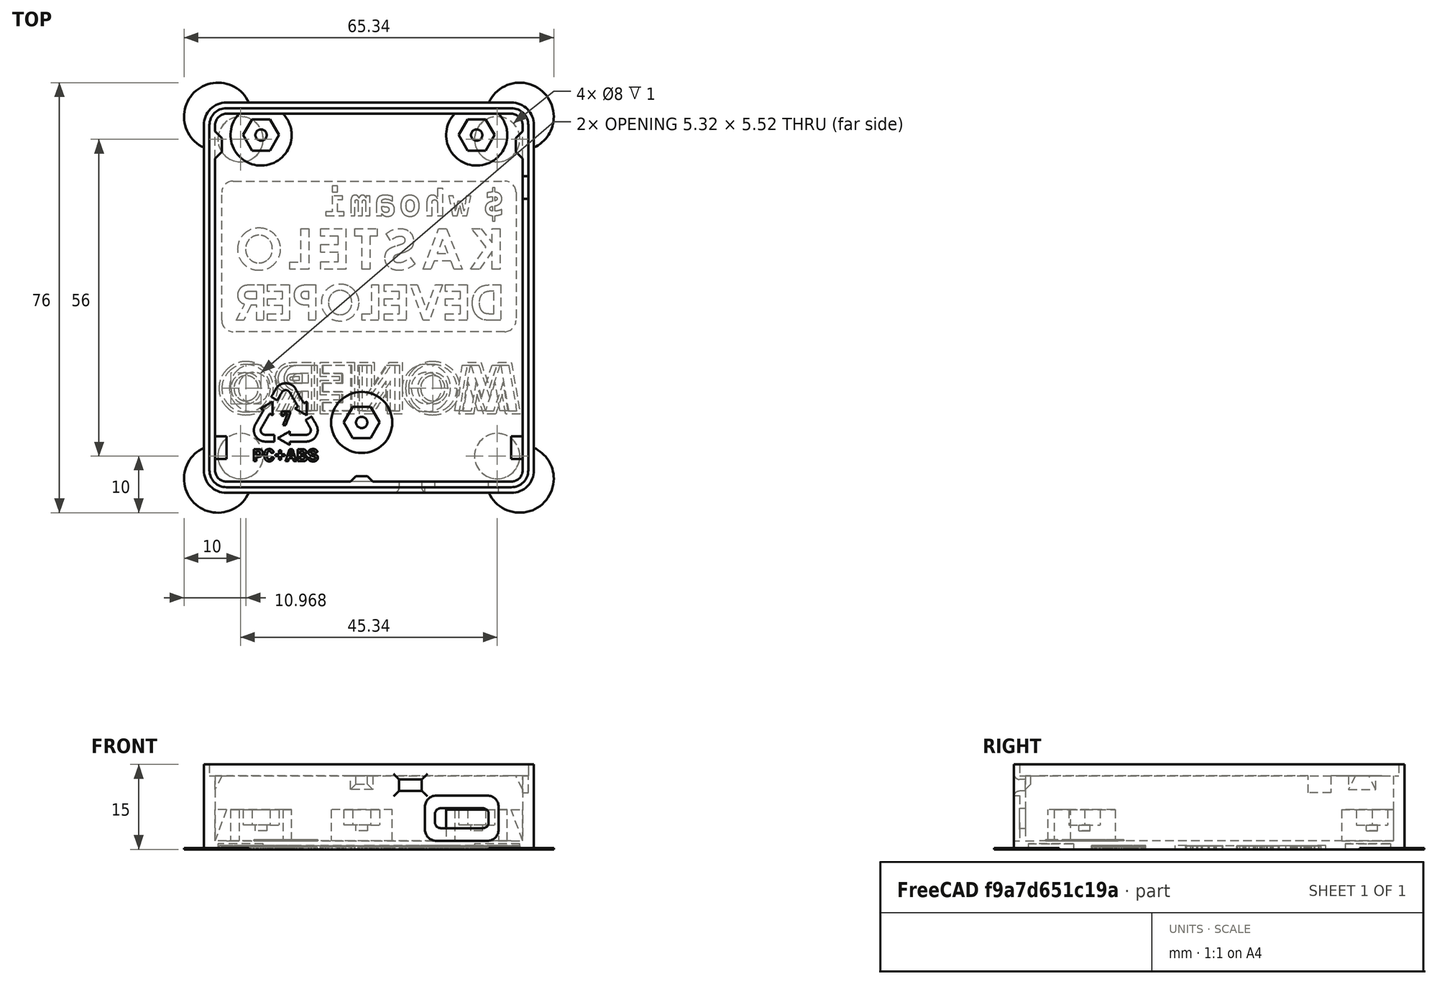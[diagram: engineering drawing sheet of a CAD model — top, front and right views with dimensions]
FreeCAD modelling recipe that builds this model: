
FCSTD DOCUMENT  (FreeCAD 0.18.3R)
Label: bneckfdmpla
License: CreativeCommons Attribution-ShareAlike
LicenseURL: http://creativecommons.org/licenses/by-sa/4.0/
objects: Sketcher::SketchObject×46, PartDesign::Pocket×29, Part::Feature×27, PartDesign::Pad×19, PartDesign::Body×14, Part::Part2DObjectPython×10, PartDesign::Fillet×6, Part::Extrusion×5, Mesh::Feature×5, App::DocumentObjectGroup×3, App::Part×3, TechDraw::DrawViewPart×3, Spreadsheet::Sheet×1, TechDraw::DrawSVGTemplate×1, TechDraw::DrawViewSymbol×1, TechDraw::DrawPage×1
note: 204 computed .brp shape members not serialized (recipe doc carries the construction recipe); baked Part::Feature solids carry a one-line shape summary decoded from their .brp

FEATURE [Sketcher::SketchObject] Sketch  label="Outline"
  MapMode = 5
  Support = -> [XY_Plane001]
  sketch-geometry (4):
    g0: LineSegment StartX=-26.67 StartY=32 StartZ=0 EndX=26.67 EndY=32 EndZ=0
    g1: LineSegment StartX=26.67 StartY=32 StartZ=0 EndX=26.67 EndY=-32 EndZ=0
    g2: LineSegment StartX=26.67 StartY=-32 StartZ=0 EndX=-26.67 EndY=-32 EndZ=0
    g3: LineSegment StartX=-26.67 StartY=-32 StartZ=0 EndX=-26.67 EndY=32 EndZ=0
  constraints (10):
    c: Coincident(g0,g1)
    c: Coincident(g1,g2)
    c: Coincident(g2,g3)
    c: Coincident(g3,g0)
    c: Horizontal(g2)
    c: Vertical(g1)
    c: DistanceY(g3,g3) = 64  'Length'
    c: DistanceX(g0,g0) = 53.34  'Width'
    c: Symmetric(g0,g0,g-2)
    c: Symmetric(g0,g2,g-1)
FEATURE [Spreadsheet::Sheet] Spreadsheet
  cells = A1=Nozzle Size; B1(nozzlesize)==0.4mm; A2=Wall Thick; B2(wallthick)==nozzlesize * 5; A3=Wall Thin; B3(wallthin)==1mm; A4=Case Length; B4(caselength)==64mm; A5=Floor Thick; B5(floorthick)==1.5mm; A6=Case Width; B6(casewidth)==53.34mm; A7=Case Height; B7(caseheight)==floorthick + batthick + pcbthick + plateclear + platethick; A8=Batt Thick; B8(batthick)==5.5mm; A9=Nut Thick; B9(nutthick)==2.7mm; A10=Nut Rad; B10(nutrad)==3.4mm; A11=Plate Clear; B11(plateclear)==4.4mm; A12=Plate Thick; B12(platethick)==2mm; A13=PCB Thick; B13(pcbthick)==1.6mm; A14=PCB Offset; B14(pcboffset)==0.5mm; A15=Skirt Height; B15(skirthick)==0.2mm
FEATURE [Sketcher::SketchObject] Sketch001  label="Outbox"
  ExternalGeometry = -> [Sketch]
  MapMode = 5
  Support = -> [XY_Plane001]
  expr: Constraints[7] = Spreadsheet.wallthick + Spreadsheet.pcboffset
  expr: Constraints[6] = Spreadsheet.wallthick + Spreadsheet.pcboffset
  sketch-geometry (4):
    g0: LineSegment StartX=-29.17 StartY=34.5 StartZ=0 EndX=29.17 EndY=34.5 EndZ=0
    g1: LineSegment StartX=29.17 StartY=34.5 StartZ=0 EndX=29.17 EndY=-34.5 EndZ=0
    g2: LineSegment StartX=29.17 StartY=-34.5 StartZ=0 EndX=-29.17 EndY=-34.5 EndZ=0
    g3: LineSegment StartX=-29.17 StartY=-34.5 StartZ=0 EndX=-29.17 EndY=34.5 EndZ=0
  constraints (10):
    c: Coincident(g0,g1)
    c: Coincident(g1,g2)
    c: Coincident(g2,g3)
    c: Coincident(g3,g0)
    c: Horizontal(g2)
    c: Vertical(g1)
    c: DistanceX(g0,g-3) = 2.5
    c: DistanceY(g-3,g0) = 2.5
    c: Symmetric(g0,g0,g-2)
    c: Symmetric(g0,g2,g-1)
FEATURE [PartDesign::Pad] Pad  label="Padmain"
  Length = 15
  Length2 = 100
  Profile = -> Sketch001
  Type = 0
  expr: Length = Spreadsheet.caseheight
FEATURE [Sketcher::SketchObject] Sketch002
  ExternalGeometry = -> [Sketch]
  MapMode = 5
  Placement = pos=(0,0,15) rot=(0,0,1;0rad)
  Support = -> [Pad]
  expr: Constraints[9] = Spreadsheet.pcboffset
  expr: Constraints[7] = Spreadsheet.pcboffset
  sketch-geometry (4):
    g0: LineSegment StartX=-27.17 StartY=32.5 StartZ=0 EndX=27.17 EndY=32.5 EndZ=0
    g1: LineSegment StartX=27.17 StartY=32.5 StartZ=0 EndX=27.17 EndY=-32.5 EndZ=0
    g2: LineSegment StartX=27.17 StartY=-32.5 StartZ=0 EndX=-27.17 EndY=-32.5 EndZ=0
    g3: LineSegment StartX=-27.17 StartY=-32.5 StartZ=0 EndX=-27.17 EndY=32.5 EndZ=0
  constraints (10):
    c: Coincident(g0,g1)
    c: Coincident(g1,g2)
    c: Coincident(g2,g3)
    c: Coincident(g3,g0)
    c: Horizontal(g2)
    c: Vertical(g1)
    c: Symmetric(g0,g0,g-2)
    c: DistanceY(g-3,g0) = 0.5
    c: Symmetric(g0,g2,g-1)
    c: DistanceX(g0,g-3) = 0.5
FEATURE [PartDesign::Pocket] Pocket  label="Pocketwallout"
  BaseFeature = -> Pad
  Length = 13.5
  Length2 = 12
  Profile = -> Sketch002
  Type = 0
  expr: Length = Padmain.Length - Spreadsheet.floorthick
FEATURE [Sketcher::SketchObject] Sketch003
  ExternalGeometry = -> [Sketch]
  MapMode = 5
  Placement = pos=(0,0,15) rot=(0,0,1;0rad)
  Support = -> [Pocket]
  expr: Constraints[9] = Spreadsheet.wallthick / 2 + Spreadsheet.pcboffset
  expr: Constraints[7] = Spreadsheet.wallthick / 2 + Spreadsheet.pcboffset
  sketch-geometry (4):
    g0: LineSegment StartX=-28.17 StartY=33.5 StartZ=0 EndX=28.17 EndY=33.5 EndZ=0
    g1: LineSegment StartX=28.17 StartY=33.5 StartZ=0 EndX=28.17 EndY=-33.5 EndZ=0
    g2: LineSegment StartX=28.17 StartY=-33.5 StartZ=0 EndX=-28.17 EndY=-33.5 EndZ=0
    g3: LineSegment StartX=-28.17 StartY=-33.5 StartZ=0 EndX=-28.17 EndY=33.5 EndZ=0
  constraints (10):
    c: Coincident(g0,g1)
    c: Coincident(g1,g2)
    c: Coincident(g2,g3)
    c: Coincident(g3,g0)
    c: Horizontal(g2)
    c: Vertical(g1)
    c: Symmetric(g0,g0,g-2)
    c: DistanceY(g-3,g0) = 1.5
    c: Symmetric(g0,g2,g-1)
    c: DistanceX(g0,g-3) = 1.5
FEATURE [PartDesign::Pocket] Pocket001  label="Pocketwallin"
  BaseFeature = -> Pocket
  Length = 2
  Length2 = 100
  Profile = -> Sketch003
  Type = 0
  expr: Length = Spreadsheet.platethick
FEATURE [TechDraw::DrawSVGTemplate] Template
  EditableTexts = Designed_by_Name=Monero Hardware; Drawing_number=1; FC-Date=December 2019; FC-SC=Scale; FC-SH=1; FC-Title=Breakneck Enclosure; Subtitle=Hardware wallet developer edition; Weight=Weight
  Height = 210
  Orientation = 1
  Width = 297
FEATURE [Sketcher::SketchObject] Sketch005
  ExternalGeometry = -> [Sketch]
  MapMode = 5
  Placement = pos=(0,-35,0) rot=(1,0,0;1.5708rad)
  expr: Constraints[18] = Spreadsheet.floorthick + Spreadsheet.batthick - 3.25mm
  sketch-geometry (8):
    g0: LineSegment StartX=12.67 StartY=7.25 StartZ=0 EndX=20.17 EndY=7.25 EndZ=0
    g1: LineSegment StartX=21.17 StartY=6.25 StartZ=0 EndX=21.17 EndY=4.75 EndZ=0
    g2: LineSegment StartX=20.17 StartY=3.75 StartZ=0 EndX=12.67 EndY=3.75 EndZ=0
    g3: LineSegment StartX=11.67 StartY=4.75 StartZ=0 EndX=11.67 EndY=6.25 EndZ=0
    g4: ArcOfCircle CenterX=12.67 CenterY=6.25 CenterZ=0 NormalX=0 NormalY=0 NormalZ=1 AngleXU=0 Radius=1 StartAngle=1.5708 EndAngle=3.14159
    g5: ArcOfCircle CenterX=12.67 CenterY=4.75 CenterZ=0 NormalX=0 NormalY=0 NormalZ=1 AngleXU=0 Radius=1 StartAngle=3.14159 EndAngle=4.71239
    g6: ArcOfCircle CenterX=20.17 CenterY=4.75 CenterZ=0 NormalX=0 NormalY=0 NormalZ=1 AngleXU=0 Radius=1 StartAngle=4.71239 EndAngle=6.28319
    g7: ArcOfCircle CenterX=20.17 CenterY=6.25 CenterZ=0 NormalX=0 NormalY=0 NormalZ=1 AngleXU=0 Radius=1 StartAngle=3e-16 EndAngle=1.5708
  constraints (20):
    c: Horizontal(g0)
    c: Horizontal(g2)
    c: Vertical(g1)
    c: Vertical(g3)
    c: Tangent(g0,g4) = 1.5708
    c: Tangent(g3,g4) = 1.5708
    c: Tangent(g3,g5) = 1.5708
    c: Tangent(g2,g5) = 1.5708
    c: Tangent(g2,g6) = 1.5708
    c: Tangent(g1,g6) = 1.5708
    c: Tangent(g1,g7) = 1.5708
    c: Tangent(g0,g7) = 1.5708
    c: Radius(g4) = 1
    c: Equal(g4,g5)
    c: Equal(g4,g6)
    c: Equal(g4,g7)
    c: DistanceY(g2,g0) = 3.5
    c: DistanceX(g3,g1) = 9.5
    c: DistanceY(g-3,g2) = 3.75
    c: DistanceX(g1,g-3) = 5.5
FEATURE [PartDesign::Pocket] Pocket002  label="Pocketusbhole"
  BaseFeature = -> Pocket001
  Length = 3
  Length2 = 100
  Profile = -> Sketch005
  Type = 0
FEATURE [Sketcher::SketchObject] Sketch007
  AttachmentOffset = pos=(0,0,10.6) rot=(0,0,1;0rad)
  ExternalGeometry = -> [Sketch]
  MapMode = 5
  Placement = pos=(0,0,10.6) rot=(0,0,1;0rad)
  Support = -> [XY_Plane001]
  expr: AttachmentOffset.Base.z = Spreadsheet.caseheight - Spreadsheet.plateclear
  sketch-geometry (12):
    g0: LineSegment StartX=-27.97 StartY=30.2 StartZ=0 EndX=-25.77 EndY=28 EndZ=0
    g1: LineSegment StartX=-25.77 StartY=28 StartZ=0 EndX=-25.77 EndY=26 EndZ=0
    g2: LineSegment StartX=-25.77 StartY=26 StartZ=0 EndX=-27.97 EndY=23.8 EndZ=0
    g3: LineSegment StartX=-27.97 StartY=23.8 StartZ=0 EndX=-27.97 EndY=30.2 EndZ=0
    g4: LineSegment StartX=25.77 StartY=28 StartZ=0 EndX=25.77 EndY=26 EndZ=0
    g5: LineSegment StartX=25.77 StartY=26 StartZ=0 EndX=27.97 EndY=23.8 EndZ=0
    g6: LineSegment StartX=27.97 StartY=23.8 StartZ=0 EndX=27.97 EndY=30.2 EndZ=0
    g7: LineSegment StartX=27.97 StartY=30.2 StartZ=0 EndX=25.77 EndY=28 EndZ=0
    g8: LineSegment StartX=-2.27 StartY=-31.55 StartZ=0 EndX=-0.27 EndY=-31.55 EndZ=0
    g9: LineSegment StartX=-0.27 StartY=-31.55 StartZ=0 EndX=1.43 EndY=-33.25 EndZ=0
    g10: LineSegment StartX=1.43 StartY=-33.25 StartZ=0 EndX=-3.97 EndY=-33.25 EndZ=0
    g11: LineSegment StartX=-3.97 StartY=-33.25 StartZ=0 EndX=-2.27 EndY=-31.55 EndZ=0
  constraints (36):
    c: Coincident(g0,g1)
    c: Vertical(g1)
    c: Coincident(g1,g2)
    c: Coincident(g2,g3)
    c: Coincident(g3,g0)
    c: DistanceY(g1,g0) = 2
    c: Angle(g0,g1) = 2.35619
    c: Angle(g1,g2) = 2.35619
    c: Vertical(g3)
    c: DistanceX(g0,g0) = 2.2
    c: Coincident(g4,g5)
    c: Coincident(g5,g6)
    c: Coincident(g6,g7)
    c: Coincident(g7,g4)
    c: DistanceY(g4,g4) = 2
    c: Vertical(g4)
    c: Angle(g4,g7) = 2.35619
    c: Angle(g5,g4) = 2.35619
    c: Vertical(g6)
    c: DistanceX(g4,g6) = 2.2
    c: Coincident(g8,g9)
    c: Coincident(g9,g10)
    c: Coincident(g10,g11)
    c: Coincident(g11,g8)
    c: Horizontal(g10)
    c: Angle(g11,g8) = 2.35619
    c: Angle(g8,g9) = 2.35619
    c: DistanceX(g8,g8) = 2
    c: DistanceY(g9,g8) = 1.7
    c: DistanceY(g0,g-3) = 4
    c: DistanceX(g-3,g0) = 0.9
    c: DistanceY(g4,g-3) = 4
    c: DistanceX(g4,g-3) = 0.9
    c: DistanceY(g-4,g8) = 0.45
    c: Horizontal(g8)
    c: DistanceX(g-4,g8) = 24.4
FEATURE [PartDesign::Pad] Pad003  label="Padshienen"
  BaseFeature = -> Pocket002
  Length = 2.4
  Length2 = 5
  Offset = 8
  Profile = -> Sketch007
  Type = 0
  expr: Length = Spreadsheet.plateclear - Spreadsheet.platethick
FEATURE [Sketcher::SketchObject] Sketch009
  ExternalGeometry = -> [Sketch003]
  MapMode = 5
  Placement = pos=(0,0,0) rot=(0.57735,0.57735,0.57735;2.0944rad)
  Support = -> [YZ_Plane001]
  expr: Constraints[9] = Spreadsheet.platethick + 2mm
  expr: Constraints[11] = Spreadsheet.platethick - 1mm
  sketch-geometry (4):
    g0: LineSegment StartX=17.5 StartY=14 StartZ=0 EndX=21.5 EndY=14 EndZ=0
    g1: LineSegment StartX=21.5 StartY=14 StartZ=0 EndX=21.5 EndY=10 EndZ=0
    g2: LineSegment StartX=21.5 StartY=10 StartZ=0 EndX=17.5 EndY=10 EndZ=0
    g3: LineSegment StartX=17.5 StartY=10 StartZ=0 EndX=17.5 EndY=14 EndZ=0
  constraints (12):
    c: Coincident(g0,g1)
    c: Coincident(g1,g2)
    c: Coincident(g2,g3)
    c: Coincident(g3,g0)
    c: Horizontal(g0)
    c: Horizontal(g2)
    c: Vertical(g1)
    c: Vertical(g3)
    c: DistanceX(g0,g0) = 4
    c: DistanceY(g2,g0) = 4
    c: DistanceX(g0,g-3) = 12
    c: DistanceY(g0,g-3) = 1
FEATURE [PartDesign::Pocket] Pocket003  label="Pocketplatrem"
  BaseFeature = -> Pad003
  Length = 28.17
  Length2 = 100
  Profile = -> Sketch009
  Reversed = true
  Type = 0
  expr: Length = Spreadsheet.casewidth / 2 + Spreadsheet.pcboffset + Spreadsheet.wallthin
FEATURE [Sketcher::SketchObject] Sketch010
  MapMode = 5
  Placement = pos=(0,0,0) rot=(1,0,0;3.14159rad)
  expr: Constraints[11] = Spreadsheet.caselength / 2
  expr: Constraints[10] = Spreadsheet.caselength / 2
  expr: Constraints[9] = Spreadsheet.caselength / 2
  expr: Constraints[8] = Spreadsheet.casewidth / 2
  expr: Constraints[7] = Spreadsheet.casewidth / 2
  expr: Constraints[6] = Spreadsheet.casewidth / 2
  expr: Constraints[1] = Spreadsheet.caselength / 2
  expr: Constraints[0] = Spreadsheet.casewidth / 2
  sketch-geometry (4):
    g0: Circle CenterX=26.67 CenterY=32 CenterZ=0 NormalX=0 NormalY=0 NormalZ=1 AngleXU=0 Radius=6
    g1: Circle CenterX=-26.67 CenterY=32 CenterZ=0 NormalX=0 NormalY=0 NormalZ=1 AngleXU=0 Radius=6
    g2: Circle CenterX=-26.67 CenterY=-32 CenterZ=0 NormalX=0 NormalY=0 NormalZ=1 AngleXU=0 Radius=6
    g3: Circle CenterX=26.67 CenterY=-32 CenterZ=0 NormalX=0 NormalY=0 NormalZ=1 AngleXU=0 Radius=6
  constraints (12):
    c: DistanceX(g-1,g0) = 26.67
    c: DistanceY(g-1,g0) = 32
    c: Radius(g0) = 6
    c: Equal(g0,g1)
    c: Equal(g1,g2)
    c: Equal(g2,g3)
    c: DistanceX(g1,g-1) = 26.67
    c: DistanceX(g2,g-1) = 26.67
    c: DistanceX(g-1,g3) = 26.67
    c: DistanceY(g2,g-1) = 32
    c: DistanceY(g3,g-1) = 32
    c: DistanceY(g-1,g1) = 32
FEATURE [PartDesign::Pad] Pad006  label="FDMBrims"
  BaseFeature = -> Pocket003
  Length = 0.2
  Length2 = 100
  Profile = -> Sketch010
  Reversed = true
  Type = 0
  expr: Length = Spreadsheet.skirthick
FEATURE [Sketcher::SketchObject] Sketch011
  ExternalGeometry = -> [Sketch]
  MapMode = 5
  Placement = pos=(0,-34.5,0) rot=(1,0,0;1.5708rad)
  expr: Constraints[18] = Spreadsheet.floorthick + Spreadsheet.batthick - 5.5mm
  sketch-geometry (8):
    g0: LineSegment StartX=11.92 StartY=9.5 StartZ=0 EndX=20.92 EndY=9.5 EndZ=0
    g1: LineSegment StartX=22.92 StartY=7.5 StartZ=0 EndX=22.92 EndY=3.5 EndZ=0
    g2: LineSegment StartX=20.92 StartY=1.5 StartZ=0 EndX=11.92 EndY=1.5 EndZ=0
    g3: LineSegment StartX=9.92 StartY=3.5 StartZ=0 EndX=9.92 EndY=7.5 EndZ=0
    g4: ArcOfCircle CenterX=11.92 CenterY=7.5 CenterZ=0 NormalX=0 NormalY=0 NormalZ=1 AngleXU=0 Radius=2 StartAngle=1.5708 EndAngle=3.14159
    g5: ArcOfCircle CenterX=20.92 CenterY=7.5 CenterZ=0 NormalX=0 NormalY=0 NormalZ=1 AngleXU=0 Radius=2 StartAngle=0 EndAngle=1.5708
    g6: ArcOfCircle CenterX=20.92 CenterY=3.5 CenterZ=0 NormalX=0 NormalY=0 NormalZ=1 AngleXU=0 Radius=2 StartAngle=4.71239 EndAngle=6.28319
    g7: ArcOfCircle CenterX=11.92 CenterY=3.5 CenterZ=0 NormalX=0 NormalY=0 NormalZ=1 AngleXU=0 Radius=2 StartAngle=3.14159 EndAngle=4.71239
  constraints (20):
    c: Horizontal(g0)
    c: Horizontal(g2)
    c: Vertical(g1)
    c: Vertical(g3)
    c: Tangent(g0,g4) = 1.5708
    c: Tangent(g3,g4) = 1.5708
    c: Tangent(g0,g5) = 1.5708
    c: Tangent(g1,g5) = 1.5708
    c: Tangent(g1,g6) = 1.5708
    c: Tangent(g2,g6) = 1.5708
    c: Tangent(g2,g7) = 1.5708
    c: Tangent(g3,g7) = 1.5708
    c: Radius(g4) = 2
    c: Equal(g4,g5)
    c: Equal(g5,g6)
    c: Equal(g6,g7)
    c: DistanceX(g0,g0) = 9
    c: DistanceY(g1,g1) = 4
    c: DistanceY(g-1,g2) = 1.5
    c: DistanceX(g1,g-3) = 3.75
FEATURE [PartDesign::Pocket] Pocket004  label="Pocketplug"
  BaseFeature = -> Pad006
  Length = 1
  Length2 = 100
  Profile = -> Sketch011
  Type = 0
FEATURE [Sketcher::SketchObject] Sketch012
  AttachmentOffset = pos=(0,0,-24) rot=(0,0,1;0rad)
  ExternalGeometry = -> [Sketch002]
  MapMode = 5
  Placement = pos=(0,24,5.3e-15) rot=(1,0,0;1.5708rad)
  Support = -> [XZ_Plane001]
  expr: Constraints[10] = Spreadsheet.caseheight - Spreadsheet.plateclear - Spreadsheet.nutthick
  expr: Constraints[9] = Spreadsheet.caseheight - Spreadsheet.plateclear
  sketch-geometry (8):
    g0: LineSegment StartX=-23.17 StartY=10.6 StartZ=0 EndX=-23.17 EndY=18.5 EndZ=0
    g1: LineSegment StartX=-23.17 StartY=18.5 StartZ=0 EndX=-27.17 EndY=10.6 EndZ=0
    g2: LineSegment StartX=-27.17 StartY=10.6 StartZ=0 EndX=-23.17 EndY=10.6 EndZ=0
    g3: Circle [constr] CenterX=-25.17 CenterY=14.55 CenterZ=0 NormalX=0 NormalY=0 NormalZ=1 AngleXU=0 Radius=4.42747
    g4: LineSegment StartX=27.17 StartY=10.6 StartZ=0 EndX=23.17 EndY=18.5 EndZ=0
    g5: LineSegment StartX=23.17 StartY=18.5 StartZ=0 EndX=23.17 EndY=10.6 EndZ=0
    g6: LineSegment StartX=23.17 StartY=10.6 StartZ=0 EndX=27.17 EndY=10.6 EndZ=0
    g7: Circle [constr] CenterX=25.17 CenterY=14.55 CenterZ=0 NormalX=0 NormalY=0 NormalZ=1 AngleXU=0 Radius=4.42747
  constraints (23):
    c: Coincident(g0,g1)
    c: Coincident(g1,g2)
    c: Coincident(g2,g0)
    c: PointOnObject(g0,g3)
    c: PointOnObject(g1,g3)
    c: PointOnObject(g2,g3)
    c: Horizontal(g2)
    c: Angle(g0,g2) = 1.5708
    c: DistanceX(g2,g2) = 4
    c: DistanceY(g-1,g0) = 10.6
    c: DistanceY(g0,g0) = 7.9
    c: Vertical(g1,g-3)
    c: Coincident(g4,g5)
    c: Coincident(g5,g6)
    c: Coincident(g6,g4)
    c: PointOnObject(g4,g7)
    c: PointOnObject(g5,g7)
    c: PointOnObject(g6,g7)
    c: Horizontal(g6)
    c: Angle(g6,g5) = 1.5708
    c: Equal(g6,g2)
    c: Equal(g5,g0)
    c: Symmetric(g5,g0,g-2)
FEATURE [PartDesign::Pocket] Pocket005  label="Pocketschienen"
  BaseFeature = -> Pocket004
  Length = 6
  Length2 = 100
  Profile = -> Sketch012
  Type = 0
FEATURE [Sketcher::SketchObject] Sketch013
  AttachmentOffset = pos=(0,0,1) rot=(0,0,1;0rad)
  ExternalGeometry = -> [Sketch007,Sketch002]
  MapMode = 5
  Placement = pos=(1,-2e-16,2e-16) rot=(0.57735,0.57735,0.57735;2.0944rad)
  Support = -> [YZ_Plane001]
  sketch-geometry (4):
    g0: LineSegment StartX=-30.5 StartY=12.6 StartZ=0 EndX=-32.5 EndY=10.6 EndZ=0
    g1: LineSegment StartX=-32.5 StartY=10.6 StartZ=0 EndX=-30.5 EndY=10.6 EndZ=0
    g2: LineSegment StartX=-30.5 StartY=10.6 StartZ=0 EndX=-30.5 EndY=12.6 EndZ=0
    g3: Circle [constr] CenterX=-31.5 CenterY=11.6 CenterZ=0 NormalX=0 NormalY=0 NormalZ=1 AngleXU=0 Radius=1.41421
  constraints (12):
    c: Coincident(g0,g1)
    c: Coincident(g1,g2)
    c: Coincident(g2,g0)
    c: PointOnObject(g0,g3)
    c: PointOnObject(g1,g3)
    c: PointOnObject(g2,g3)
    c: Horizontal(g1)
    c: Angle(g2,g1) = 1.5708
    c: DistanceX(g1,g1) = 2
    c: DistanceY(g2,g2) = 2
    c: PointOnObject(g-3,g1)
    c: Vertical(g-4,g0)
FEATURE [PartDesign::Pocket] Pocket006  label="Pocketschienund"
  BaseFeature = -> Pocket005
  Length = 4.5
  Length2 = 100
  Profile = -> Sketch013
  Type = 0
FEATURE [Sketcher::SketchObject] Sketch014
  AttachmentOffset = pos=(0,0,7) rot=(0,0,1;0rad)
  ExternalGeometry = -> [Sketch002]
  Placement = pos=(0,0,1.5) rot=(0,0,1;0rad)
  Support = -> [XY_Plane001]
  expr: Placement.Base.z = Spreadsheet.floorthick
  expr: AttachmentOffset.Base.z = Spreadsheet.floorthick + Spreadsheet.batthick
  sketch-geometry (8):
    g0: LineSegment StartX=25.17 StartY=-24.5 StartZ=0 EndX=27.17 EndY=-24.5 EndZ=0
    g1: LineSegment StartX=27.17 StartY=-24.5 StartZ=0 EndX=27.17 EndY=-28.5 EndZ=0
    g2: LineSegment StartX=27.17 StartY=-28.5 StartZ=0 EndX=25.17 EndY=-28.5 EndZ=0
    g3: LineSegment StartX=25.17 StartY=-28.5 StartZ=0 EndX=25.17 EndY=-24.5 EndZ=0
    g4: LineSegment StartX=-27.17 StartY=-24.5 StartZ=0 EndX=-25.17 EndY=-24.5 EndZ=0
    g5: LineSegment StartX=-25.17 StartY=-24.5 StartZ=0 EndX=-25.17 EndY=-28.5 EndZ=0
    g6: LineSegment StartX=-25.17 StartY=-28.5 StartZ=0 EndX=-27.17 EndY=-28.5 EndZ=0
    g7: LineSegment StartX=-27.17 StartY=-28.5 StartZ=0 EndX=-27.17 EndY=-24.5 EndZ=0
  constraints (23):
    c: Coincident(g0,g1)
    c: Coincident(g1,g2)
    c: Coincident(g2,g3)
    c: Coincident(g3,g0)
    c: Horizontal(g0)
    c: Horizontal(g2)
    c: Vertical(g1)
    c: Vertical(g3)
    c: Coincident(g4,g5)
    c: Coincident(g5,g6)
    c: Coincident(g6,g7)
    c: Coincident(g7,g4)
    c: Horizontal(g4)
    c: Horizontal(g6)
    c: Vertical(g5)
    c: Vertical(g7)
    c: DistanceY(g3,g3) = 4
    c: DistanceX(g0,g0) = 2
    c: PointOnObject(g0,g-3)
    c: DistanceY(g-3,g1) = 4
    c: Equal(g1,g5)
    c: Equal(g0,g4)
    c: Symmetric(g5,g2,g-2)
FEATURE [Sketcher::SketchObject] Sketch016
  MapMode = 5
  Support = -> [XY_Plane001]
  sketch-geometry (4):
    g0: Circle CenterX=-22.67 CenterY=28 CenterZ=0 NormalX=0 NormalY=0 NormalZ=1 AngleXU=0 Radius=4
    g1: Circle CenterX=22.67 CenterY=28 CenterZ=0 NormalX=0 NormalY=0 NormalZ=1 AngleXU=0 Radius=4
    g2: Circle CenterX=-22.67 CenterY=-28 CenterZ=0 NormalX=0 NormalY=0 NormalZ=1 AngleXU=0 Radius=4
    g3: Circle CenterX=22.67 CenterY=-28 CenterZ=0 NormalX=0 NormalY=0 NormalZ=1 AngleXU=0 Radius=4
  constraints (9):
    c: Radius(g0) = 4
    c: Radius(g1) = 4
    c: Radius(g2) = 4
    c: Radius(g3) = 4
    c: DistanceY(g3,g-1) = 28
    c: DistanceX(g-1,g3) = 22.67
    c: Symmetric(g3,g2,g-2)
    c: Symmetric(g3,g1,g-1)
    c: Symmetric(g1,g0,g-2)
FEATURE [Sketcher::SketchObject] Sketch017
  AttachmentOffset = pos=(0,0,32) rot=(0,0,1;0rad)
  MapMode = 5
  Placement = pos=(0,-32,-7.1e-15) rot=(1,0,0;1.5708rad)
  Support = -> [XZ_Plane001]
  expr: Constraints[11] = Spreadsheet.floorthick + Spreadsheet.batthick + Spreadsheet.pcbthick + 1.75mm
  sketch-geometry (4):
    g0: LineSegment StartX=5.35 StartY=12.35 StartZ=0 EndX=9.35 EndY=12.35 EndZ=0
    g1: LineSegment StartX=9.35 StartY=12.35 StartZ=0 EndX=9.35 EndY=10.35 EndZ=0
    g2: LineSegment StartX=9.35 StartY=10.35 StartZ=0 EndX=5.35 EndY=10.35 EndZ=0
    g3: LineSegment StartX=5.35 StartY=10.35 StartZ=0 EndX=5.35 EndY=12.35 EndZ=0
  constraints (12):
    c: Coincident(g0,g1)
    c: Coincident(g1,g2)
    c: Coincident(g2,g3)
    c: Coincident(g3,g0)
    c: Horizontal(g0)
    c: Horizontal(g2)
    c: Vertical(g1)
    c: Vertical(g3)
    c: DistanceX(g2,g2) = 4
    c: DistanceY(g3,g3) = 2
    c: DistanceX(g2,g-1) = -5.35
    c: DistanceY(g-1,g2) = 10.35
FEATURE [PartDesign::Pocket] Pocket009  label="Pwrswtchpockt"
  BaseFeature = -> Pocket006
  Length = 3
  Length2 = 100
  Profile = -> Sketch017
  Reversed = true
  Type = 0
FEATURE [Sketcher::SketchObject] Sketch018
  MapMode = 5
  Support = -> [XY_Plane001]
  sketch-geometry (4):
    g0: LineSegment StartX=-26 StartY=20.6 StartZ=0 EndX=26 EndY=20.6 EndZ=0
    g1: LineSegment StartX=26 StartY=20.6 StartZ=0 EndX=26 EndY=-6 EndZ=0
    g2: LineSegment StartX=26 StartY=-6 StartZ=0 EndX=-26 EndY=-6 EndZ=0
    g3: LineSegment StartX=-26 StartY=-6 StartZ=0 EndX=-26 EndY=20.6 EndZ=0
  constraints (11):
    c: Coincident(g0,g1)
    c: Coincident(g1,g2)
    c: Coincident(g2,g3)
    c: Coincident(g3,g0)
    c: DistanceY(g3,g3) = 26.6
    c: DistanceX(g2,g2) = 52
    c: Vertical(g3)
    c: Vertical(g1)
    c: Horizontal(g0)
    c: Symmetric(g2,g1,g-2)
    c: DistanceY(g2,g-1) = 6
FEATURE [PartDesign::Pocket] Pocket010  label="Etikepockt"
  BaseFeature = -> Pocket009
  Length = 0.65
  Length2 = 100
  Profile = -> Sketch018
  Reversed = true
  Type = 0
FEATURE [PartDesign::Pocket] Pocket011  label="Bumppockt"
  BaseFeature = -> Pocket010
  Length = 1
  Length2 = 100
  Profile = -> Sketch016
  Reversed = true
  Type = 0
FEATURE [TechDraw::DrawViewSymbol] Symbol  label="Monerotxt"
  LockPosition = false
  Rotation = 0
  ScaleType = 2
  Symbol = <blob: 2754 chars omitted>
  X = 210.556
  Y = 33.5011
FEATURE [Sketcher::SketchObject] Sketch019
  MapMode = 5
  Support = -> [XY_Plane003]
  sketch-geometry (4):
    g0: LineSegment StartX=-26 StartY=20.6 StartZ=0 EndX=26 EndY=20.6 EndZ=0
    g1: LineSegment StartX=26 StartY=20.6 StartZ=0 EndX=26 EndY=-6 EndZ=0
    g2: LineSegment StartX=26 StartY=-6 StartZ=0 EndX=-26 EndY=-6 EndZ=0
    g3: LineSegment StartX=-26 StartY=-6 StartZ=0 EndX=-26 EndY=20.6 EndZ=0
  constraints (11):
    c: Coincident(g0,g1)
    c: Coincident(g1,g2)
    c: Coincident(g2,g3)
    c: Coincident(g3,g0)
    c: Horizontal(g0)
    c: Vertical(g1)
    c: Vertical(g3)
    c: DistanceY(g2,g-1) = 6
    c: DistanceY(g3,g3) = 26.6
    c: DistanceX(g2,g2) = 52
    c: Symmetric(g2,g1,g-2)
FEATURE [PartDesign::Pad] Pad008  label="Etikepad"
  Length = 0.65
  Length2 = 100
  Profile = -> Sketch019
  Type = 0
FEATURE [PartDesign::Fillet] Fillet002  label="Etikepadfil"
  Base = -> Pad008 [Edge2,Edge1,Edge8,Edge5]
  BaseFeature = -> Pad008
  Radius = 2
FEATURE [Part::Part2DObjectPython] ShapeString  label="Shapestrin-0,4mm"  # Draft 2D object (typed FeaturePython)
  FontFile = <userpath>/Downloads/MoneroGothic_v3.otf
  Placement = pos=(25,-20,0) rot=(0,1,0;3.14159rad)
  Size = 4.5
  String = MONERO
  Tracking = 0
FEATURE [Part::Part2DObjectPython] ShapeString001  label="Shapestrout"  # Draft 2D object (typed FeaturePython)
  FontFile = <userpath>/Downloads/MoneroGothic_v3.otf
  Placement = pos=(25,-20,0) rot=(0,1,0;3.14159rad)
  Size = 4.5
  String = MONERO
  Tracking = 0
FEATURE [Part::Extrusion] Extrude  label="Textstringtrude"
  Base = -> ShapeString001
  Dir = (0,0,-1)
  DirMode = 2
  FaceMakerClass = Part::FaceMakerBullseye
  LengthFwd = 0
  LengthRev = 0.4
  Solid = true
  Symmetric = false
FEATURE [Part::Part2DObjectPython] ShapeString002  label="Shapewhoami"  # Draft 2D object (typed FeaturePython)
  FontFile = <userpath>/Downloads/DejaVuSansMono-Bold.ttf
  Placement = pos=(18,14.5,0) rot=(0,1,0;3.14159rad)
  Size = 5
  String = whoami
  Tracking = 0.5
FEATURE [Part::Part2DObjectPython] ShapeString003  label="Shapekastelo"  # Draft 2D object (typed FeaturePython)
  FontFile = <userpath>/Downloads/MoneroGothic_v3.otf
  Placement = pos=(24,5,0) rot=(0,1,0;3.14159rad)
  Size = 4
  String = KASTELO
  Tracking = 1
FEATURE [Part::Part2DObjectPython] ShapeString004  label="Shapedevkit"  # Draft 2D object (typed FeaturePython)
  FontFile = <userpath>/Downloads/MoneroGothic_v3.otf
  Placement = pos=(24,-4,0) rot=(0,1,0;3.14159rad)
  Size = 3.5
  String = DEVELOPER
  Tracking = 0
FEATURE [PartDesign::Pocket] Pocket013  label="Whoamipock"
  BaseFeature = -> Fillet002
  Length = 0.6
  Length2 = 100
  Profile = -> ShapeString002
  Type = 0
FEATURE [PartDesign::Pocket] Pocket014  label="Kastelopock"
  BaseFeature = -> Pocket013
  Length = 0.6
  Length2 = 100
  Profile = -> ShapeString003
  Type = 0
FEATURE [PartDesign::Pocket] Pocket015  label="Developock"
  BaseFeature = -> Pocket014
  Length = 0.6
  Length2 = 100
  Profile = -> ShapeString004
  Type = 0
FEATURE [Part::Part2DObjectPython] ShapeString005  label="Strshawhoami"  # Draft 2D object (typed FeaturePython)
  FontFile = <userpath>/Downloads/DejaVuSansMono-Bold.ttf
  Placement = pos=(18,14.5,0) rot=(0,1,0;3.14159rad)
  Size = 5
  String = whoami
  Tracking = 0.5
FEATURE [Part::Part2DObjectPython] ShapeString006  label="Strshakastelo"  # Draft 2D object (typed FeaturePython)
  FontFile = <userpath>/Downloads/MoneroGothic_v3.otf
  Placement = pos=(24,5,0) rot=(0,1,0;3.14159rad)
  Size = 4
  String = KASTELO
  Tracking = 1
FEATURE [Part::Part2DObjectPython] ShapeString007  label="Strshadevelop"  # Draft 2D object (typed FeaturePython)
  FontFile = <userpath>/Downloads/MoneroGothic_v3.otf
  Placement = pos=(24,-4,0) rot=(0,1,0;3.14159rad)
  Size = 3.5
  String = DEVELOPER
  Tracking = 0
FEATURE [Part::Part2DObjectPython] ShapeString008  label="Shapedollar"  # Draft 2D object (typed FeaturePython)
  FontFile = <userpath>/Downloads/DejaVuSansMono-Bold.ttf
  Placement = pos=(24,14.5,0) rot=(0,1,0;3.14159rad)
  Size = 5
  String = $
  Tracking = 0
FEATURE [Part::Part2DObjectPython] ShapeString009  label="Strshadollar"  # Draft 2D object (typed FeaturePython)
  FontFile = <userpath>/Downloads/DejaVuSansMono-Bold.ttf
  Placement = pos=(24,14.5,0) rot=(0,1,0;3.14159rad)
  Size = 5
  String = $
  Tracking = 0
FEATURE [PartDesign::Pocket] Pocket016  label="Dollarpock"
  BaseFeature = -> Pocket015
  Length = 0.6
  Length2 = 100
  Profile = -> ShapeString008
  Type = 0
FEATURE [PartDesign::Body] Body001  label="Bodyetik"
  Group = -> [Sketch019,Pad008,Fillet002,ShapeString002,ShapeString003,ShapeString004,Pocket013,Pocket014,Pocket015,ShapeString008,Pocket016]
  Origin = -> Origin003
  Tip = -> Pocket016
FEATURE [Part::Extrusion] Extrude001  label="Textwhotrude"
  Base = -> ShapeString005
  Dir = (0,0,-1)
  DirMode = 2
  FaceMakerClass = Part::FaceMakerBullseye
  LengthFwd = 0
  LengthRev = 0.6
  Solid = true
  Symmetric = false
FEATURE [Part::Extrusion] Extrude002  label="Textkastrude"
  Base = -> ShapeString006
  Dir = (0,0,-1)
  DirMode = 2
  FaceMakerClass = Part::FaceMakerBullseye
  LengthFwd = 0
  LengthRev = 0.6
  Solid = true
  Symmetric = false
FEATURE [Part::Extrusion] Extrude003  label="Textdevtrude"
  Base = -> ShapeString007
  Dir = (0,0,-1)
  DirMode = 2
  FaceMakerClass = Part::FaceMakerBullseye
  LengthFwd = 0
  LengthRev = 0.6
  Solid = true
  Symmetric = false
FEATURE [Part::Extrusion] Extrude004  label="Textquestrude"
  Base = -> ShapeString009
  Dir = (0,0,-1)
  DirMode = 2
  FaceMakerClass = Part::FaceMakerBullseye
  LengthFwd = 0
  LengthRev = 0.6
  Solid = true
  Symmetric = false
FEATURE [Sketcher::SketchObject] Sketch075  label="Sktchorigmontxt"
  Placement = pos=(0,0,0) rot=(0,0,1;3.14159rad)
  sketch-geometry (90):
    g0: BSplineCurve PolesCount=4 KnotsCount=2 Degree=3 IsPeriodic=0
    g1: BSplineCurve PolesCount=4 KnotsCount=2 Degree=3 IsPeriodic=0
    g2: BSplineCurve PolesCount=4 KnotsCount=2 Degree=3 IsPeriodic=0
    g3: BSplineCurve PolesCount=4 KnotsCount=2 Degree=3 IsPeriodic=0
    g4: BSplineCurve PolesCount=4 KnotsCount=2 Degree=3 IsPeriodic=0
    g5: BSplineCurve PolesCount=4 KnotsCount=2 Degree=3 IsPeriodic=0
    g6: BSplineCurve PolesCount=4 KnotsCount=2 Degree=3 IsPeriodic=0
    g7: BSplineCurve PolesCount=4 KnotsCount=2 Degree=3 IsPeriodic=0
    g8: BSplineCurve PolesCount=4 KnotsCount=2 Degree=3 IsPeriodic=0
    g9: BSplineCurve PolesCount=4 KnotsCount=2 Degree=3 IsPeriodic=0
    g10: BSplineCurve PolesCount=4 KnotsCount=2 Degree=3 IsPeriodic=0
    g11: BSplineCurve PolesCount=4 KnotsCount=2 Degree=3 IsPeriodic=0
    g12: BSplineCurve PolesCount=4 KnotsCount=2 Degree=3 IsPeriodic=0
    g13: BSplineCurve PolesCount=4 KnotsCount=2 Degree=3 IsPeriodic=0
    g14: BSplineCurve PolesCount=4 KnotsCount=2 Degree=3 IsPeriodic=0
    g15: BSplineCurve PolesCount=4 KnotsCount=2 Degree=3 IsPeriodic=0
    g16: BSplineCurve PolesCount=4 KnotsCount=2 Degree=3 IsPeriodic=0
    g17: BSplineCurve PolesCount=2 KnotsCount=2 Degree=1 IsPeriodic=0
    g18: BSplineCurve PolesCount=2 KnotsCount=2 Degree=1 IsPeriodic=0
    g19: BSplineCurve PolesCount=4 KnotsCount=2 Degree=3 IsPeriodic=0
    g20: BSplineCurve PolesCount=4 KnotsCount=2 Degree=3 IsPeriodic=0
    g21: BSplineCurve PolesCount=4 KnotsCount=2 Degree=3 IsPeriodic=0
    g22: BSplineCurve PolesCount=4 KnotsCount=2 Degree=3 IsPeriodic=0
    g23: BSplineCurve PolesCount=4 KnotsCount=2 Degree=3 IsPeriodic=0
    g24: BSplineCurve PolesCount=2 KnotsCount=2 Degree=1 IsPeriodic=0
    g25: BSplineCurve PolesCount=2 KnotsCount=2 Degree=1 IsPeriodic=0
    g26: BSplineCurve PolesCount=2 KnotsCount=2 Degree=1 IsPeriodic=0
    g27: BSplineCurve PolesCount=2 KnotsCount=2 Degree=1 IsPeriodic=0
    g28: BSplineCurve PolesCount=2 KnotsCount=2 Degree=1 IsPeriodic=0
    g29: BSplineCurve PolesCount=2 KnotsCount=2 Degree=1 IsPeriodic=0
    g30: BSplineCurve PolesCount=2 KnotsCount=2 Degree=1 IsPeriodic=0
    g31: BSplineCurve PolesCount=2 KnotsCount=2 Degree=1 IsPeriodic=0
    g32: BSplineCurve PolesCount=4 KnotsCount=2 Degree=3 IsPeriodic=0
    g33: BSplineCurve PolesCount=4 KnotsCount=2 Degree=3 IsPeriodic=0
    g34: BSplineCurve PolesCount=4 KnotsCount=2 Degree=3 IsPeriodic=0
    g35: BSplineCurve PolesCount=4 KnotsCount=2 Degree=3 IsPeriodic=0
    g36: BSplineCurve PolesCount=4 KnotsCount=2 Degree=3 IsPeriodic=0
    g37: BSplineCurve PolesCount=2 KnotsCount=2 Degree=1 IsPeriodic=0
    g38: BSplineCurve PolesCount=2 KnotsCount=2 Degree=1 IsPeriodic=0
    g39: BSplineCurve PolesCount=2 KnotsCount=2 Degree=1 IsPeriodic=0
    g40: BSplineCurve PolesCount=2 KnotsCount=2 Degree=1 IsPeriodic=0
    g41: BSplineCurve PolesCount=2 KnotsCount=2 Degree=1 IsPeriodic=0
    g42: BSplineCurve PolesCount=2 KnotsCount=2 Degree=1 IsPeriodic=0
    g43: BSplineCurve PolesCount=2 KnotsCount=2 Degree=1 IsPeriodic=0
    g44: BSplineCurve PolesCount=2 KnotsCount=2 Degree=1 IsPeriodic=0
    g45: BSplineCurve PolesCount=2 KnotsCount=2 Degree=1 IsPeriodic=0
    g46: BSplineCurve PolesCount=2 KnotsCount=2 Degree=1 IsPeriodic=0
    g47: BSplineCurve PolesCount=2 KnotsCount=2 Degree=1 IsPeriodic=0
    g48: BSplineCurve PolesCount=2 KnotsCount=2 Degree=1 IsPeriodic=0
    g49: BSplineCurve PolesCount=2 KnotsCount=2 Degree=1 IsPeriodic=0
    g50: BSplineCurve PolesCount=2 KnotsCount=2 Degree=1 IsPeriodic=0
    g51: BSplineCurve PolesCount=2 KnotsCount=2 Degree=1 IsPeriodic=0
    g52: BSplineCurve PolesCount=2 KnotsCount=2 Degree=1 IsPeriodic=0
    g53: BSplineCurve PolesCount=2 KnotsCount=2 Degree=1 IsPeriodic=0
    g54: BSplineCurve PolesCount=2 KnotsCount=2 Degree=1 IsPeriodic=0
    g55: BSplineCurve PolesCount=2 KnotsCount=2 Degree=1 IsPeriodic=0
    g56: BSplineCurve PolesCount=2 KnotsCount=2 Degree=1 IsPeriodic=0
    g57: BSplineCurve PolesCount=2 KnotsCount=2 Degree=1 IsPeriodic=0
    g58: BSplineCurve PolesCount=2 KnotsCount=2 Degree=1 IsPeriodic=0
    g59: BSplineCurve PolesCount=2 KnotsCount=2 Degree=1 IsPeriodic=0
    g60: BSplineCurve PolesCount=4 KnotsCount=2 Degree=3 IsPeriodic=0
    g61: BSplineCurve PolesCount=4 KnotsCount=2 Degree=3 IsPeriodic=0
    g62: BSplineCurve PolesCount=4 KnotsCount=2 Degree=3 IsPeriodic=0
    g63: BSplineCurve PolesCount=4 KnotsCount=2 Degree=3 IsPeriodic=0
    g64: BSplineCurve PolesCount=4 KnotsCount=2 Degree=3 IsPeriodic=0
    g65: BSplineCurve PolesCount=4 KnotsCount=2 Degree=3 IsPeriodic=0
    g66: BSplineCurve PolesCount=4 KnotsCount=2 Degree=3 IsPeriodic=0
    g67: BSplineCurve PolesCount=4 KnotsCount=2 Degree=3 IsPeriodic=0
    g68: BSplineCurve PolesCount=4 KnotsCount=2 Degree=3 IsPeriodic=0
    g69: BSplineCurve PolesCount=4 KnotsCount=2 Degree=3 IsPeriodic=0
    g70: BSplineCurve PolesCount=4 KnotsCount=2 Degree=3 IsPeriodic=0
    g71: BSplineCurve PolesCount=4 KnotsCount=2 Degree=3 IsPeriodic=0
    g72: BSplineCurve PolesCount=4 KnotsCount=2 Degree=3 IsPeriodic=0
    g73: BSplineCurve PolesCount=4 KnotsCount=2 Degree=3 IsPeriodic=0
    g74: BSplineCurve PolesCount=4 KnotsCount=2 Degree=3 IsPeriodic=0
    g75: BSplineCurve PolesCount=4 KnotsCount=2 Degree=3 IsPeriodic=0
    g76: BSplineCurve PolesCount=4 KnotsCount=2 Degree=3 IsPeriodic=0
    g77: BSplineCurve PolesCount=2 KnotsCount=2 Degree=1 IsPeriodic=0
    g78: BSplineCurve PolesCount=2 KnotsCount=2 Degree=1 IsPeriodic=0
    g79: BSplineCurve PolesCount=2 KnotsCount=2 Degree=1 IsPeriodic=0
    g80: BSplineCurve PolesCount=2 KnotsCount=2 Degree=1 IsPeriodic=0
    g81: BSplineCurve PolesCount=2 KnotsCount=2 Degree=1 IsPeriodic=0
    g82: BSplineCurve PolesCount=2 KnotsCount=2 Degree=1 IsPeriodic=0
    g83: BSplineCurve PolesCount=2 KnotsCount=2 Degree=1 IsPeriodic=0
    g84: BSplineCurve PolesCount=2 KnotsCount=2 Degree=1 IsPeriodic=0
    g85: BSplineCurve PolesCount=2 KnotsCount=2 Degree=1 IsPeriodic=0
    g86: BSplineCurve PolesCount=2 KnotsCount=2 Degree=1 IsPeriodic=0
    g87: BSplineCurve PolesCount=2 KnotsCount=2 Degree=1 IsPeriodic=0
    g88: BSplineCurve PolesCount=2 KnotsCount=2 Degree=1 IsPeriodic=0
    g89: BSplineCurve PolesCount=2 KnotsCount=2 Degree=1 IsPeriodic=0
  constraints (90):
    c: Coincident(g0,g1)
    c: Coincident(g1,g2)
    c: Coincident(g2,g3)
    c: Coincident(g3,g4)
    c: Coincident(g4,g5)
    c: Coincident(g5,g6)
    c: Coincident(g6,g7)
    c: Coincident(g7,g0)
    c: Coincident(g8,g9)
    c: Coincident(g9,g10)
    c: Coincident(g10,g11)
    c: Coincident(g11,g12)
    c: Coincident(g12,g13)
    c: Coincident(g13,g14)
    c: Coincident(g14,g15)
    c: Coincident(g15,g16)
    c: Coincident(g16,g8)
    c: Coincident(g17,g18)
    c: Coincident(g18,g19)
    c: Coincident(g19,g20)
    c: Coincident(g20,g21)
    c: Coincident(g21,g22)
    c: Coincident(g22,g23)
    c: Coincident(g23,g24)
    c: Coincident(g24,g17)
    c: Coincident(g25,g26)
    c: Coincident(g26,g27)
    c: Coincident(g27,g28)
    c: Coincident(g28,g29)
    c: Coincident(g29,g30)
    c: Coincident(g30,g31)
    c: Coincident(g31,g32)
    c: Coincident(g32,g33)
    c: Coincident(g33,g34)
    c: Coincident(g34,g35)
    c: Coincident(g35,g36)
    c: Coincident(g36,g37)
    c: Coincident(g37,g25)
    c: Coincident(g38,g39)
    c: Coincident(g39,g40)
    c: Coincident(g40,g41)
    c: Coincident(g41,g42)
    c: Coincident(g42,g43)
    c: Coincident(g43,g44)
    c: Coincident(g44,g45)
    c: Coincident(g45,g46)
    c: Coincident(g46,g47)
    c: Coincident(g47,g48)
    c: Coincident(g48,g49)
    c: Coincident(g49,g38)
    c: Coincident(g50,g51)
    c: Coincident(g51,g52)
    c: Coincident(g52,g53)
    c: Coincident(g53,g54)
    c: Coincident(g54,g55)
    c: Coincident(g55,g56)
    c: Coincident(g56,g57)
    c: Coincident(g57,g58)
    c: Coincident(g58,g59)
    c: Coincident(g59,g50)
    c: Coincident(g60,g61)
    c: Coincident(g61,g62)
    c: Coincident(g62,g63)
    c: Coincident(g63,g64)
    c: Coincident(g64,g65)
    c: Coincident(g65,g66)
    c: Coincident(g66,g67)
    c: Coincident(g67,g60)
    c: Coincident(g68,g69)
    c: Coincident(g69,g70)
    c: Coincident(g70,g71)
    c: Coincident(g71,g72)
    c: Coincident(g72,g73)
    c: Coincident(g73,g74)
    c: Coincident(g74,g75)
    c: Coincident(g75,g76)
    c: Coincident(g76,g68)
    c: Coincident(g77,g78)
    c: Coincident(g78,g79)
    c: Coincident(g79,g80)
    c: Coincident(g80,g81)
    c: Coincident(g81,g82)
    c: Coincident(g82,g83)
    c: Coincident(g83,g84)
    c: Coincident(g84,g85)
    c: Coincident(g85,g86)
    c: Coincident(g86,g87)
    c: Coincident(g87,g88)
    c: Coincident(g88,g89)
    c: Coincident(g89,g77)
FEATURE [Part::Feature] path262
  Placement = pos=(-25.87,-11,0) rot=(0,0,1;0rad)
  shape: bbox 9.55 x 8.105 x 2e-07 mm, 0 faces, 0 solids (baked)
FEATURE [Part::Feature] path264
  Placement = pos=(-25.87,-11,0) rot=(0,0,1;0rad)
  shape: bbox 8.422 x 8.512 x 2e-07 mm, 0 faces, 0 solids (baked)
FEATURE [Part::Feature] path264001
  Placement = pos=(-25.87,-11,0) rot=(0,0,1;0rad)
  shape: bbox 5.317 x 5.52 x 2e-07 mm, 0 faces, 0 solids (baked)
FEATURE [Part::Feature] path266
  Placement = pos=(-25.87,-11,0) rot=(0,0,1;0rad)
  shape: bbox 6.491 x 8.105 x 2e-07 mm, 0 faces, 0 solids (baked)
FEATURE [Part::Feature] path268
  Placement = pos=(-25.87,-11,0) rot=(0,0,1;0rad)
  shape: bbox 4.99 x 8.105 x 2e-07 mm, 0 faces, 0 solids (baked)
FEATURE [Part::Feature] path270
  Placement = pos=(-25.87,-11,0) rot=(0,0,1;0rad)
  shape: bbox 6.209 x 8.117 x 2e-07 mm, 0 faces, 0 solids (baked)
FEATURE [Part::Feature] path270001
  Placement = pos=(-25.87,-11,0) rot=(0,0,1;0rad)
  shape: bbox 2.788 x 1.648 x 2e-07 mm, 0 faces, 0 solids (baked)
FEATURE [Part::Feature] path272
  Placement = pos=(-25.87,-11,0) rot=(0,0,1;0rad)
  shape: bbox 8.422 x 8.512 x 2e-07 mm, 0 faces, 0 solids (baked)
FEATURE [Part::Feature] path272001
  Placement = pos=(-25.87,-11,0) rot=(0,0,1;0rad)
  shape: bbox 5.317 x 5.52 x 2e-07 mm, 0 faces, 0 solids (baked)
FEATURE [Sketcher::SketchObject] Sketch098
  Placement = pos=(0,0,0) rot=(0,0,1;3.14159rad)
  sketch-geometry (13):
    g0: BSplineCurve PolesCount=2 KnotsCount=2 Degree=1 IsPeriodic=0
    g1: BSplineCurve PolesCount=2 KnotsCount=2 Degree=1 IsPeriodic=0
    g2: BSplineCurve PolesCount=2 KnotsCount=2 Degree=1 IsPeriodic=0
    g3: BSplineCurve PolesCount=2 KnotsCount=2 Degree=1 IsPeriodic=0
    g4: BSplineCurve PolesCount=2 KnotsCount=2 Degree=1 IsPeriodic=0
    g5: BSplineCurve PolesCount=2 KnotsCount=2 Degree=1 IsPeriodic=0
    g6: BSplineCurve PolesCount=2 KnotsCount=2 Degree=1 IsPeriodic=0
    g7: BSplineCurve PolesCount=2 KnotsCount=2 Degree=1 IsPeriodic=0
    g8: BSplineCurve PolesCount=2 KnotsCount=2 Degree=1 IsPeriodic=0
    g9: BSplineCurve PolesCount=2 KnotsCount=2 Degree=1 IsPeriodic=0
    g10: BSplineCurve PolesCount=2 KnotsCount=2 Degree=1 IsPeriodic=0
    g11: BSplineCurve PolesCount=2 KnotsCount=2 Degree=1 IsPeriodic=0
    g12: BSplineCurve PolesCount=2 KnotsCount=2 Degree=1 IsPeriodic=0
  constraints (13):
    c: Coincident(g0,g1)
    c: Coincident(g1,g2)
    c: Coincident(g2,g3)
    c: Coincident(g3,g4)
    c: Coincident(g4,g5)
    c: Coincident(g5,g6)
    c: Coincident(g6,g7)
    c: Coincident(g7,g8)
    c: Coincident(g8,g9)
    c: Coincident(g9,g10)
    c: Coincident(g10,g11)
    c: Coincident(g11,g12)
    c: Coincident(g12,g0)
FEATURE [Sketcher::SketchObject] Sketch104
  Placement = pos=(0,0,0) rot=(0,0,1;3.14159rad)
  sketch-geometry (10):
    g0: BSplineCurve PolesCount=2 KnotsCount=2 Degree=1 IsPeriodic=0
    g1: BSplineCurve PolesCount=2 KnotsCount=2 Degree=1 IsPeriodic=0
    g2: BSplineCurve PolesCount=2 KnotsCount=2 Degree=1 IsPeriodic=0
    g3: BSplineCurve PolesCount=2 KnotsCount=2 Degree=1 IsPeriodic=0
    g4: BSplineCurve PolesCount=2 KnotsCount=2 Degree=1 IsPeriodic=0
    g5: BSplineCurve PolesCount=2 KnotsCount=2 Degree=1 IsPeriodic=0
    g6: BSplineCurve PolesCount=2 KnotsCount=2 Degree=1 IsPeriodic=0
    g7: BSplineCurve PolesCount=2 KnotsCount=2 Degree=1 IsPeriodic=0
    g8: BSplineCurve PolesCount=2 KnotsCount=2 Degree=1 IsPeriodic=0
    g9: BSplineCurve PolesCount=2 KnotsCount=2 Degree=1 IsPeriodic=0
  constraints (10):
    c: Coincident(g0,g1)
    c: Coincident(g1,g2)
    c: Coincident(g2,g3)
    c: Coincident(g3,g4)
    c: Coincident(g4,g5)
    c: Coincident(g5,g6)
    c: Coincident(g6,g7)
    c: Coincident(g7,g8)
    c: Coincident(g8,g9)
    c: Coincident(g9,g0)
FEATURE [Sketcher::SketchObject] Sketch105
  Placement = pos=(0,0,0) rot=(0,0,1;3.14159rad)
  sketch-geometry (12):
    g0: BSplineCurve PolesCount=2 KnotsCount=2 Degree=1 IsPeriodic=0
    g1: BSplineCurve PolesCount=2 KnotsCount=2 Degree=1 IsPeriodic=0
    g2: BSplineCurve PolesCount=2 KnotsCount=2 Degree=1 IsPeriodic=0
    g3: BSplineCurve PolesCount=2 KnotsCount=2 Degree=1 IsPeriodic=0
    g4: BSplineCurve PolesCount=2 KnotsCount=2 Degree=1 IsPeriodic=0
    g5: BSplineCurve PolesCount=2 KnotsCount=2 Degree=1 IsPeriodic=0
    g6: BSplineCurve PolesCount=2 KnotsCount=2 Degree=1 IsPeriodic=0
    g7: BSplineCurve PolesCount=2 KnotsCount=2 Degree=1 IsPeriodic=0
    g8: BSplineCurve PolesCount=2 KnotsCount=2 Degree=1 IsPeriodic=0
    g9: BSplineCurve PolesCount=2 KnotsCount=2 Degree=1 IsPeriodic=0
    g10: BSplineCurve PolesCount=2 KnotsCount=2 Degree=1 IsPeriodic=0
    g11: BSplineCurve PolesCount=2 KnotsCount=2 Degree=1 IsPeriodic=0
  constraints (12):
    c: Coincident(g0,g1)
    c: Coincident(g1,g2)
    c: Coincident(g2,g3)
    c: Coincident(g3,g4)
    c: Coincident(g4,g5)
    c: Coincident(g5,g6)
    c: Coincident(g6,g7)
    c: Coincident(g7,g8)
    c: Coincident(g8,g9)
    c: Coincident(g9,g10)
    c: Coincident(g10,g11)
    c: Coincident(g11,g0)
FEATURE [Sketcher::SketchObject] Sketch107
  Placement = pos=(0,0,0) rot=(0,0,1;3.14159rad)
  sketch-geometry (17):
    g0: BSplineCurve PolesCount=4 KnotsCount=2 Degree=3 IsPeriodic=0
    g1: BSplineCurve PolesCount=4 KnotsCount=2 Degree=3 IsPeriodic=0
    g2: BSplineCurve PolesCount=4 KnotsCount=2 Degree=3 IsPeriodic=0
    g3: BSplineCurve PolesCount=4 KnotsCount=2 Degree=3 IsPeriodic=0
    g4: BSplineCurve PolesCount=4 KnotsCount=2 Degree=3 IsPeriodic=0
    g5: BSplineCurve PolesCount=4 KnotsCount=2 Degree=3 IsPeriodic=0
    g6: BSplineCurve PolesCount=4 KnotsCount=2 Degree=3 IsPeriodic=0
    g7: BSplineCurve PolesCount=4 KnotsCount=2 Degree=3 IsPeriodic=0
    g8: BSplineCurve PolesCount=4 KnotsCount=2 Degree=3 IsPeriodic=0
    g9: BSplineCurve PolesCount=4 KnotsCount=2 Degree=3 IsPeriodic=0
    g10: BSplineCurve PolesCount=4 KnotsCount=2 Degree=3 IsPeriodic=0
    g11: BSplineCurve PolesCount=4 KnotsCount=2 Degree=3 IsPeriodic=0
    g12: BSplineCurve PolesCount=4 KnotsCount=2 Degree=3 IsPeriodic=0
    g13: BSplineCurve PolesCount=4 KnotsCount=2 Degree=3 IsPeriodic=0
    g14: BSplineCurve PolesCount=4 KnotsCount=2 Degree=3 IsPeriodic=0
    g15: BSplineCurve PolesCount=4 KnotsCount=2 Degree=3 IsPeriodic=0
    g16: BSplineCurve PolesCount=4 KnotsCount=2 Degree=3 IsPeriodic=0
  constraints (17):
    c: Coincident(g0,g1)
    c: Coincident(g1,g2)
    c: Coincident(g2,g3)
    c: Coincident(g3,g4)
    c: Coincident(g4,g5)
    c: Coincident(g5,g6)
    c: Coincident(g6,g7)
    c: Coincident(g7,g0)
    c: Coincident(g8,g9)
    c: Coincident(g9,g10)
    c: Coincident(g10,g11)
    c: Coincident(g11,g12)
    c: Coincident(g12,g13)
    c: Coincident(g13,g14)
    c: Coincident(g14,g15)
    c: Coincident(g15,g16)
    c: Coincident(g16,g8)
FEATURE [Sketcher::SketchObject] Sketch108
  Placement = pos=(0,0,0) rot=(0,0,1;3.14159rad)
  sketch-geometry (17):
    g0: BSplineCurve PolesCount=4 KnotsCount=2 Degree=3 IsPeriodic=0
    g1: BSplineCurve PolesCount=4 KnotsCount=2 Degree=3 IsPeriodic=0
    g2: BSplineCurve PolesCount=4 KnotsCount=2 Degree=3 IsPeriodic=0
    g3: BSplineCurve PolesCount=4 KnotsCount=2 Degree=3 IsPeriodic=0
    g4: BSplineCurve PolesCount=4 KnotsCount=2 Degree=3 IsPeriodic=0
    g5: BSplineCurve PolesCount=4 KnotsCount=2 Degree=3 IsPeriodic=0
    g6: BSplineCurve PolesCount=4 KnotsCount=2 Degree=3 IsPeriodic=0
    g7: BSplineCurve PolesCount=4 KnotsCount=2 Degree=3 IsPeriodic=0
    g8: BSplineCurve PolesCount=4 KnotsCount=2 Degree=3 IsPeriodic=0
    g9: BSplineCurve PolesCount=4 KnotsCount=2 Degree=3 IsPeriodic=0
    g10: BSplineCurve PolesCount=4 KnotsCount=2 Degree=3 IsPeriodic=0
    g11: BSplineCurve PolesCount=4 KnotsCount=2 Degree=3 IsPeriodic=0
    g12: BSplineCurve PolesCount=4 KnotsCount=2 Degree=3 IsPeriodic=0
    g13: BSplineCurve PolesCount=4 KnotsCount=2 Degree=3 IsPeriodic=0
    g14: BSplineCurve PolesCount=4 KnotsCount=2 Degree=3 IsPeriodic=0
    g15: BSplineCurve PolesCount=4 KnotsCount=2 Degree=3 IsPeriodic=0
    g16: BSplineCurve PolesCount=4 KnotsCount=2 Degree=3 IsPeriodic=0
  constraints (17):
    c: Coincident(g0,g1)
    c: Coincident(g1,g2)
    c: Coincident(g2,g3)
    c: Coincident(g3,g4)
    c: Coincident(g4,g5)
    c: Coincident(g5,g6)
    c: Coincident(g6,g7)
    c: Coincident(g7,g0)
    c: Coincident(g8,g9)
    c: Coincident(g9,g10)
    c: Coincident(g10,g11)
    c: Coincident(g11,g12)
    c: Coincident(g12,g13)
    c: Coincident(g13,g14)
    c: Coincident(g14,g15)
    c: Coincident(g15,g16)
    c: Coincident(g16,g8)
FEATURE [Sketcher::SketchObject] Sketch109
  Placement = pos=(0,0,0) rot=(0,0,1;3.14159rad)
  sketch-geometry (21):
    g0: BSplineCurve PolesCount=2 KnotsCount=2 Degree=1 IsPeriodic=0
    g1: BSplineCurve PolesCount=2 KnotsCount=2 Degree=1 IsPeriodic=0
    g2: BSplineCurve PolesCount=4 KnotsCount=2 Degree=3 IsPeriodic=0
    g3: BSplineCurve PolesCount=4 KnotsCount=2 Degree=3 IsPeriodic=0
    g4: BSplineCurve PolesCount=4 KnotsCount=2 Degree=3 IsPeriodic=0
    g5: BSplineCurve PolesCount=4 KnotsCount=2 Degree=3 IsPeriodic=0
    g6: BSplineCurve PolesCount=4 KnotsCount=2 Degree=3 IsPeriodic=0
    g7: BSplineCurve PolesCount=2 KnotsCount=2 Degree=1 IsPeriodic=0
    g8: BSplineCurve PolesCount=2 KnotsCount=2 Degree=1 IsPeriodic=0
    g9: BSplineCurve PolesCount=2 KnotsCount=2 Degree=1 IsPeriodic=0
    g10: BSplineCurve PolesCount=2 KnotsCount=2 Degree=1 IsPeriodic=0
    g11: BSplineCurve PolesCount=2 KnotsCount=2 Degree=1 IsPeriodic=0
    g12: BSplineCurve PolesCount=2 KnotsCount=2 Degree=1 IsPeriodic=0
    g13: BSplineCurve PolesCount=2 KnotsCount=2 Degree=1 IsPeriodic=0
    g14: BSplineCurve PolesCount=2 KnotsCount=2 Degree=1 IsPeriodic=0
    g15: BSplineCurve PolesCount=4 KnotsCount=2 Degree=3 IsPeriodic=0
    g16: BSplineCurve PolesCount=4 KnotsCount=2 Degree=3 IsPeriodic=0
    g17: BSplineCurve PolesCount=4 KnotsCount=2 Degree=3 IsPeriodic=0
    g18: BSplineCurve PolesCount=4 KnotsCount=2 Degree=3 IsPeriodic=0
    g19: BSplineCurve PolesCount=4 KnotsCount=2 Degree=3 IsPeriodic=0
    g20: BSplineCurve PolesCount=2 KnotsCount=2 Degree=1 IsPeriodic=0
  constraints (21):
    c: Coincident(g0,g1)
    c: Coincident(g1,g2)
    c: Coincident(g2,g3)
    c: Coincident(g3,g4)
    c: Coincident(g4,g5)
    c: Coincident(g5,g6)
    c: Coincident(g6,g7)
    c: Coincident(g7,g0)
    c: Coincident(g8,g9)
    c: Coincident(g9,g10)
    c: Coincident(g10,g11)
    c: Coincident(g11,g12)
    c: Coincident(g12,g13)
    c: Coincident(g13,g14)
    c: Coincident(g14,g15)
    c: Coincident(g15,g16)
    c: Coincident(g16,g17)
    c: Coincident(g17,g18)
    c: Coincident(g18,g19)
    c: Coincident(g19,g20)
    c: Coincident(g20,g8)
FEATURE [Part::Feature] path44
  Placement = pos=(-25.8125,-11,0) rot=(0,0,1;0rad)
  shape: bbox 10.49 x 8.898 x 2e-07 mm, 0 faces, 0 solids (baked)
FEATURE [Part::Feature] path46
  Placement = pos=(-25.8125,-11,0) rot=(0,0,1;0rad)
  shape: bbox 9.215 x 9.305 x 2e-07 mm, 0 faces, 0 solids (baked)
FEATURE [Part::Feature] path46001
  Placement = pos=(-25.8125,-11,0) rot=(0,0,1;0rad)
  shape: bbox 4.524 x 4.726 x 2e-07 mm, 0 faces, 0 solids (baked)
FEATURE [Part::Feature] path48
  Placement = pos=(-25.8125,-11,0) rot=(0,0,1;0rad)
  shape: bbox 7.285 x 8.898 x 2e-07 mm, 0 faces, 0 solids (baked)
FEATURE [Part::Feature] path50
  Placement = pos=(-25.8125,-11,0) rot=(0,0,1;0rad)
  shape: bbox 5.784 x 8.898 x 2e-07 mm, 0 faces, 0 solids (baked)
FEATURE [Part::Feature] path52
  Placement = pos=(-25.8125,-11,0) rot=(0,0,1;0rad)
  shape: bbox 7.268 x 8.91 x 2e-07 mm, 0 faces, 0 solids (baked)
FEATURE [Part::Feature] path52001
  Placement = pos=(-25.8125,-11,0) rot=(0,0,1;0rad)
  shape: bbox 1.994 x 0.8532 x 2e-07 mm, 0 faces, 0 solids (baked)
FEATURE [Part::Feature] path54
  Placement = pos=(-25.8125,-11,0) rot=(0,0,1;0rad)
  shape: bbox 9.217 x 9.305 x 2e-07 mm, 0 faces, 0 solids (baked)
FEATURE [Part::Feature] path54001
  Placement = pos=(-25.8125,-11,0) rot=(0,0,1;0rad)
  shape: bbox 4.523 x 4.726 x 2e-07 mm, 0 faces, 0 solids (baked)
FEATURE [App::DocumentObjectGroup] Group  label="Pathsoutext-3px"
  Group = -> [path44,path46,path46001,path48,path50,path52,path52001,path54,path54001]
FEATURE [App::DocumentObjectGroup] Group001  label="Pathsintext-0px"
  Group = -> [path262,path264,path264001,path266,path268,path270,path270001,path272,path272001]
FEATURE [Part::Feature] path864
  Placement = pos=(-25.786,-11,0) rot=(0,0,1;0rad)
  shape: bbox 10.81 x 9.164 x 2e-07 mm, 0 faces, 0 solids (baked)
FEATURE [Part::Feature] path866
  Placement = pos=(-25.786,-11,0) rot=(0,0,1;0rad)
  shape: bbox 9.481 x 9.571 x 2e-07 mm, 0 faces, 0 solids (baked)
FEATURE [Part::Feature] path866001
  Placement = pos=(-25.786,-11,0) rot=(0,0,1;0rad)
  shape: bbox 4.26 x 4.461 x 2e-07 mm, 0 faces, 0 solids (baked)
FEATURE [Part::Feature] path868
  Placement = pos=(-25.786,-11,0) rot=(0,0,1;0rad)
  shape: bbox 7.551 x 9.164 x 2e-07 mm, 0 faces, 0 solids (baked)
FEATURE [Part::Feature] path870
  Placement = pos=(-25.786,-11,0) rot=(0,0,1;0rad)
  shape: bbox 6.049 x 9.164 x 2e-07 mm, 0 faces, 0 solids (baked)
FEATURE [Part::Feature] path872
  Placement = pos=(-25.786,-11,0) rot=(0,0,1;0rad)
  shape: bbox 7.621 x 9.176 x 2e-07 mm, 0 faces, 0 solids (baked)
FEATURE [Part::Feature] path872001
  Placement = pos=(-25.786,-11,0) rot=(0,0,1;0rad)
  shape: bbox 1.731 x 0.5897 x 2e-07 mm, 0 faces, 0 solids (baked)
FEATURE [Part::Feature] path874
  Placement = pos=(-25.786,-11,0) rot=(0,0,1;0rad)
  shape: bbox 9.479 x 9.571 x 2e-07 mm, 0 faces, 0 solids (baked)
FEATURE [Part::Feature] path874001
  Placement = pos=(-25.786,-11,0) rot=(0,0,1;0rad)
  shape: bbox 4.26 x 4.461 x 2e-07 mm, 0 faces, 0 solids (baked)
FEATURE [App::DocumentObjectGroup] Group002  label="Pathsoutext-4px"
  Group = -> [path864,path866,path866001,path868,path870,path872,path872001,path874,path874001]
FEATURE [Sketcher::SketchObject] Sketch126
  Placement = pos=(0,0,0) rot=(0,0,1;3.14159rad)
  sketch-geometry (13):
    g0: BSplineCurve PolesCount=4 KnotsCount=2 Degree=3 IsPeriodic=0
    g1: BSplineCurve PolesCount=2 KnotsCount=2 Degree=1 IsPeriodic=0
    g2: BSplineCurve PolesCount=2 KnotsCount=2 Degree=1 IsPeriodic=0
    g3: BSplineCurve PolesCount=2 KnotsCount=2 Degree=1 IsPeriodic=0
    g4: BSplineCurve PolesCount=2 KnotsCount=2 Degree=1 IsPeriodic=0
    g5: BSplineCurve PolesCount=2 KnotsCount=2 Degree=1 IsPeriodic=0
    g6: BSplineCurve PolesCount=2 KnotsCount=2 Degree=1 IsPeriodic=0
    g7: BSplineCurve PolesCount=2 KnotsCount=2 Degree=1 IsPeriodic=0
    g8: BSplineCurve PolesCount=2 KnotsCount=2 Degree=1 IsPeriodic=0
    g9: BSplineCurve PolesCount=2 KnotsCount=2 Degree=1 IsPeriodic=0
    g10: BSplineCurve PolesCount=2 KnotsCount=2 Degree=1 IsPeriodic=0
    g11: BSplineCurve PolesCount=2 KnotsCount=2 Degree=1 IsPeriodic=0
    g12: BSplineCurve PolesCount=2 KnotsCount=2 Degree=1 IsPeriodic=0
  constraints (13):
    c: Coincident(g0,g1)
    c: Coincident(g1,g2)
    c: Coincident(g2,g3)
    c: Coincident(g3,g4)
    c: Coincident(g4,g5)
    c: Coincident(g5,g6)
    c: Coincident(g6,g7)
    c: Coincident(g7,g8)
    c: Coincident(g8,g9)
    c: Coincident(g9,g10)
    c: Coincident(g10,g11)
    c: Coincident(g11,g12)
    c: Coincident(g12,g0)
FEATURE [Sketcher::SketchObject] Sketch128
  Placement = pos=(0,0,0) rot=(0,0,1;3.14159rad)
  sketch-geometry (12):
    g0: BSplineCurve PolesCount=4 KnotsCount=2 Degree=3 IsPeriodic=0
    g1: BSplineCurve PolesCount=2 KnotsCount=2 Degree=1 IsPeriodic=0
    g2: BSplineCurve PolesCount=2 KnotsCount=2 Degree=1 IsPeriodic=0
    g3: BSplineCurve PolesCount=2 KnotsCount=2 Degree=1 IsPeriodic=0
    g4: BSplineCurve PolesCount=2 KnotsCount=2 Degree=1 IsPeriodic=0
    g5: BSplineCurve PolesCount=2 KnotsCount=2 Degree=1 IsPeriodic=0
    g6: BSplineCurve PolesCount=2 KnotsCount=2 Degree=1 IsPeriodic=0
    g7: BSplineCurve PolesCount=2 KnotsCount=2 Degree=1 IsPeriodic=0
    g8: BSplineCurve PolesCount=2 KnotsCount=2 Degree=1 IsPeriodic=0
    g9: BSplineCurve PolesCount=2 KnotsCount=2 Degree=1 IsPeriodic=0
    g10: BSplineCurve PolesCount=2 KnotsCount=2 Degree=1 IsPeriodic=0
    g11: BSplineCurve PolesCount=2 KnotsCount=2 Degree=1 IsPeriodic=0
  constraints (12):
    c: Coincident(g0,g1)
    c: Coincident(g1,g2)
    c: Coincident(g2,g3)
    c: Coincident(g3,g4)
    c: Coincident(g4,g5)
    c: Coincident(g5,g6)
    c: Coincident(g6,g7)
    c: Coincident(g7,g8)
    c: Coincident(g8,g9)
    c: Coincident(g9,g10)
    c: Coincident(g10,g11)
    c: Coincident(g11,g0)
FEATURE [Sketcher::SketchObject] Sketch131
  Placement = pos=(0,0,0) rot=(0,0,1;3.14159rad)
  sketch-geometry (10):
    g0: BSplineCurve PolesCount=4 KnotsCount=2 Degree=3 IsPeriodic=0
    g1: BSplineCurve PolesCount=2 KnotsCount=2 Degree=1 IsPeriodic=0
    g2: BSplineCurve PolesCount=2 KnotsCount=2 Degree=1 IsPeriodic=0
    g3: BSplineCurve PolesCount=2 KnotsCount=2 Degree=1 IsPeriodic=0
    g4: BSplineCurve PolesCount=2 KnotsCount=2 Degree=1 IsPeriodic=0
    g5: BSplineCurve PolesCount=2 KnotsCount=2 Degree=1 IsPeriodic=0
    g6: BSplineCurve PolesCount=2 KnotsCount=2 Degree=1 IsPeriodic=0
    g7: BSplineCurve PolesCount=2 KnotsCount=2 Degree=1 IsPeriodic=0
    g8: BSplineCurve PolesCount=2 KnotsCount=2 Degree=1 IsPeriodic=0
    g9: BSplineCurve PolesCount=2 KnotsCount=2 Degree=1 IsPeriodic=0
  constraints (10):
    c: Coincident(g0,g1)
    c: Coincident(g1,g2)
    c: Coincident(g2,g3)
    c: Coincident(g3,g4)
    c: Coincident(g4,g5)
    c: Coincident(g5,g6)
    c: Coincident(g6,g7)
    c: Coincident(g7,g8)
    c: Coincident(g8,g9)
    c: Coincident(g9,g0)
FEATURE [Sketcher::SketchObject] Sketch133
  Placement = pos=(0,0,0) rot=(0,0,1;3.14159rad)
  sketch-geometry (24):
    g0: BSplineCurve PolesCount=4 KnotsCount=2 Degree=3 IsPeriodic=0
    g1: BSplineCurve PolesCount=4 KnotsCount=2 Degree=3 IsPeriodic=0
    g2: BSplineCurve PolesCount=4 KnotsCount=2 Degree=3 IsPeriodic=0
    g3: BSplineCurve PolesCount=4 KnotsCount=2 Degree=3 IsPeriodic=0
    g4: BSplineCurve PolesCount=4 KnotsCount=2 Degree=3 IsPeriodic=0
    g5: BSplineCurve PolesCount=2 KnotsCount=2 Degree=1 IsPeriodic=0
    g6: BSplineCurve PolesCount=4 KnotsCount=2 Degree=3 IsPeriodic=0
    g7: BSplineCurve PolesCount=4 KnotsCount=2 Degree=3 IsPeriodic=0
    g8: BSplineCurve PolesCount=4 KnotsCount=2 Degree=3 IsPeriodic=0
    g9: BSplineCurve PolesCount=2 KnotsCount=2 Degree=1 IsPeriodic=0
    g10: BSplineCurve PolesCount=4 KnotsCount=2 Degree=3 IsPeriodic=0
    g11: BSplineCurve PolesCount=4 KnotsCount=2 Degree=3 IsPeriodic=0
    g12: BSplineCurve PolesCount=4 KnotsCount=2 Degree=3 IsPeriodic=0
    g13: BSplineCurve PolesCount=4 KnotsCount=2 Degree=3 IsPeriodic=0
    g14: BSplineCurve PolesCount=4 KnotsCount=2 Degree=3 IsPeriodic=0
    g15: BSplineCurve PolesCount=4 KnotsCount=2 Degree=3 IsPeriodic=0
    g16: BSplineCurve PolesCount=4 KnotsCount=2 Degree=3 IsPeriodic=0
    g17: BSplineCurve PolesCount=4 KnotsCount=2 Degree=3 IsPeriodic=0
    g18: BSplineCurve PolesCount=4 KnotsCount=2 Degree=3 IsPeriodic=0
    g19: BSplineCurve PolesCount=4 KnotsCount=2 Degree=3 IsPeriodic=0
    g20: BSplineCurve PolesCount=2 KnotsCount=2 Degree=1 IsPeriodic=0
    g21: BSplineCurve PolesCount=2 KnotsCount=2 Degree=1 IsPeriodic=0
    g22: BSplineCurve PolesCount=4 KnotsCount=2 Degree=3 IsPeriodic=0
    g23: BSplineCurve PolesCount=2 KnotsCount=2 Degree=1 IsPeriodic=0
  constraints (24):
    c: Coincident(g0,g1)
    c: Coincident(g1,g2)
    c: Coincident(g2,g3)
    c: Coincident(g3,g4)
    c: Coincident(g4,g5)
    c: Coincident(g5,g6)
    c: Coincident(g6,g7)
    c: Coincident(g7,g8)
    c: Coincident(g8,g9)
    c: Coincident(g9,g0)
    c: Coincident(g10,g11)
    c: Coincident(g11,g12)
    c: Coincident(g12,g13)
    c: Coincident(g13,g14)
    c: Coincident(g14,g15)
    c: Coincident(g15,g16)
    c: Coincident(g16,g17)
    c: Coincident(g17,g18)
    c: Coincident(g18,g19)
    c: Coincident(g19,g20)
    c: Coincident(g20,g21)
    c: Coincident(g21,g22)
    c: Coincident(g22,g23)
    c: Coincident(g23,g10)
FEATURE [Sketcher::SketchObject] Sketch134
  Placement = pos=(0,0,0) rot=(0,0,1;3.14159rad)
  sketch-geometry (25):
    g0: BSplineCurve PolesCount=4 KnotsCount=2 Degree=3 IsPeriodic=0
    g1: BSplineCurve PolesCount=4 KnotsCount=2 Degree=3 IsPeriodic=0
    g2: BSplineCurve PolesCount=4 KnotsCount=2 Degree=3 IsPeriodic=0
    g3: BSplineCurve PolesCount=4 KnotsCount=2 Degree=3 IsPeriodic=0
    g4: BSplineCurve PolesCount=4 KnotsCount=2 Degree=3 IsPeriodic=0
    g5: BSplineCurve PolesCount=4 KnotsCount=2 Degree=3 IsPeriodic=0
    g6: BSplineCurve PolesCount=4 KnotsCount=2 Degree=3 IsPeriodic=0
    g7: BSplineCurve PolesCount=4 KnotsCount=2 Degree=3 IsPeriodic=0
    g8: BSplineCurve PolesCount=4 KnotsCount=2 Degree=3 IsPeriodic=0
    g9: BSplineCurve PolesCount=4 KnotsCount=2 Degree=3 IsPeriodic=0
    g10: BSplineCurve PolesCount=2 KnotsCount=2 Degree=1 IsPeriodic=0
    g11: BSplineCurve PolesCount=2 KnotsCount=2 Degree=1 IsPeriodic=0
    g12: BSplineCurve PolesCount=4 KnotsCount=2 Degree=3 IsPeriodic=0
    g13: BSplineCurve PolesCount=2 KnotsCount=2 Degree=1 IsPeriodic=0
    g14: BSplineCurve PolesCount=4 KnotsCount=2 Degree=3 IsPeriodic=0
    g15: BSplineCurve PolesCount=4 KnotsCount=2 Degree=3 IsPeriodic=0
    g16: BSplineCurve PolesCount=4 KnotsCount=2 Degree=3 IsPeriodic=0
    g17: BSplineCurve PolesCount=4 KnotsCount=2 Degree=3 IsPeriodic=0
    g18: BSplineCurve PolesCount=4 KnotsCount=2 Degree=3 IsPeriodic=0
    g19: BSplineCurve PolesCount=2 KnotsCount=2 Degree=1 IsPeriodic=0
    g20: BSplineCurve PolesCount=2 KnotsCount=2 Degree=1 IsPeriodic=0
    g21: BSplineCurve PolesCount=4 KnotsCount=2 Degree=3 IsPeriodic=0
    g22: BSplineCurve PolesCount=4 KnotsCount=2 Degree=3 IsPeriodic=0
    g23: BSplineCurve PolesCount=4 KnotsCount=2 Degree=3 IsPeriodic=0
    g24: BSplineCurve PolesCount=2 KnotsCount=2 Degree=1 IsPeriodic=0
  constraints (25):
    c: Coincident(g0,g1)
    c: Coincident(g1,g2)
    c: Coincident(g2,g3)
    c: Coincident(g3,g4)
    c: Coincident(g4,g5)
    c: Coincident(g5,g6)
    c: Coincident(g6,g7)
    c: Coincident(g7,g8)
    c: Coincident(g8,g9)
    c: Coincident(g9,g10)
    c: Coincident(g10,g11)
    c: Coincident(g11,g12)
    c: Coincident(g12,g13)
    c: Coincident(g13,g0)
    c: Coincident(g14,g15)
    c: Coincident(g15,g16)
    c: Coincident(g16,g17)
    c: Coincident(g17,g18)
    c: Coincident(g18,g19)
    c: Coincident(g19,g20)
    c: Coincident(g20,g21)
    c: Coincident(g21,g22)
    c: Coincident(g22,g23)
    c: Coincident(g23,g24)
    c: Coincident(g24,g14)
FEATURE [Sketcher::SketchObject] Sketch135
  Placement = pos=(0,0,0) rot=(0,0,1;3.14159rad)
  sketch-geometry (29):
    g0: BSplineCurve PolesCount=2 KnotsCount=2 Degree=1 IsPeriodic=0
    g1: BSplineCurve PolesCount=4 KnotsCount=2 Degree=3 IsPeriodic=0
    g2: BSplineCurve PolesCount=2 KnotsCount=2 Degree=1 IsPeriodic=0
    g3: BSplineCurve PolesCount=2 KnotsCount=2 Degree=1 IsPeriodic=0
    g4: BSplineCurve PolesCount=2 KnotsCount=2 Degree=1 IsPeriodic=0
    g5: BSplineCurve PolesCount=2 KnotsCount=2 Degree=1 IsPeriodic=0
    g6: BSplineCurve PolesCount=2 KnotsCount=2 Degree=1 IsPeriodic=0
    g7: BSplineCurve PolesCount=2 KnotsCount=2 Degree=1 IsPeriodic=0
    g8: BSplineCurve PolesCount=4 KnotsCount=2 Degree=3 IsPeriodic=0
    g9: BSplineCurve PolesCount=4 KnotsCount=2 Degree=3 IsPeriodic=0
    g10: BSplineCurve PolesCount=4 KnotsCount=2 Degree=3 IsPeriodic=0
    g11: BSplineCurve PolesCount=2 KnotsCount=2 Degree=1 IsPeriodic=0
    g12: BSplineCurve PolesCount=2 KnotsCount=2 Degree=1 IsPeriodic=0
    g13: BSplineCurve PolesCount=4 KnotsCount=2 Degree=3 IsPeriodic=0
    g14: BSplineCurve PolesCount=2 KnotsCount=2 Degree=1 IsPeriodic=0
    g15: BSplineCurve PolesCount=2 KnotsCount=2 Degree=1 IsPeriodic=0
    g16: BSplineCurve PolesCount=4 KnotsCount=2 Degree=3 IsPeriodic=0
    g17: BSplineCurve PolesCount=2 KnotsCount=2 Degree=1 IsPeriodic=0
    g18: BSplineCurve PolesCount=2 KnotsCount=2 Degree=1 IsPeriodic=0
    g19: BSplineCurve PolesCount=4 KnotsCount=2 Degree=3 IsPeriodic=0
    g20: BSplineCurve PolesCount=4 KnotsCount=2 Degree=3 IsPeriodic=0
    g21: BSplineCurve PolesCount=4 KnotsCount=2 Degree=3 IsPeriodic=0
    g22: BSplineCurve PolesCount=4 KnotsCount=2 Degree=3 IsPeriodic=0
    g23: BSplineCurve PolesCount=4 KnotsCount=2 Degree=3 IsPeriodic=0
    g24: BSplineCurve PolesCount=2 KnotsCount=2 Degree=1 IsPeriodic=0
    g25: BSplineCurve PolesCount=2 KnotsCount=2 Degree=1 IsPeriodic=0
    g26: BSplineCurve PolesCount=4 KnotsCount=2 Degree=3 IsPeriodic=0
    g27: BSplineCurve PolesCount=2 KnotsCount=2 Degree=1 IsPeriodic=0
    g28: BSplineCurve PolesCount=2 KnotsCount=2 Degree=1 IsPeriodic=0
  constraints (29):
    c: Coincident(g0,g1)
    c: Coincident(g1,g2)
    c: Coincident(g2,g3)
    c: Coincident(g3,g4)
    c: Coincident(g4,g5)
    c: Coincident(g5,g6)
    c: Coincident(g6,g7)
    c: Coincident(g7,g8)
    c: Coincident(g8,g9)
    c: Coincident(g9,g10)
    c: Coincident(g10,g11)
    c: Coincident(g11,g12)
    c: Coincident(g12,g13)
    c: Coincident(g13,g14)
    c: Coincident(g14,g15)
    c: Coincident(g15,g16)
    c: Coincident(g16,g17)
    c: Coincident(g17,g0)
    c: Coincident(g18,g19)
    c: Coincident(g19,g20)
    c: Coincident(g20,g21)
    c: Coincident(g21,g22)
    c: Coincident(g22,g23)
    c: Coincident(g23,g24)
    c: Coincident(g24,g25)
    c: Coincident(g25,g26)
    c: Coincident(g26,g27)
    c: Coincident(g27,g28)
    c: Coincident(g28,g18)
FEATURE [PartDesign::Pad] Pad009
  Length = 0.65
  Length2 = 100
  Placement = pos=(0,0,0) rot=(0,0,1;3.14159rad)
  Profile = -> Sketch126
  Type = 0
FEATURE [PartDesign::Pocket] Pocket039
  BaseFeature = -> Pad009
  Length = 0.6
  Length2 = 100
  Placement = pos=(0,0,0) rot=(0,0,1;3.14159rad)
  Profile = -> Sketch098
  Reversed = true
  Type = 0
FEATURE [PartDesign::Body] Body002  label="BodyM1"
  Group = -> [Sketch098,Sketch126,Pad009,Pocket039]
  Origin = -> Origin004
  Placement = pos=(1.25,0,0) rot=(0,0,1;0rad)
  Tip = -> Pocket039
FEATURE [PartDesign::Pad] Pad010
  Length = 0.65
  Length2 = 100
  Placement = pos=(0,0,0) rot=(0,0,1;3.14159rad)
  Profile = -> Sketch133
  Type = 0
FEATURE [PartDesign::Pocket] Pocket040
  BaseFeature = -> Pad010
  Length = 0.6
  Length2 = 100
  Placement = pos=(0,0,0) rot=(0,0,1;3.14159rad)
  Profile = -> Sketch108
  Reversed = true
  Type = 0
FEATURE [PartDesign::Body] Body003  label="BodyO1"
  Group = -> [Sketch108,Sketch133,Pad010,Pocket040]
  Origin = -> Origin005
  Placement = pos=(1,0,0) rot=(0,0,1;0rad)
  Tip = -> Pocket040
FEATURE [PartDesign::Pad] Pad011
  Length = 0.65
  Length2 = 100
  Placement = pos=(0,0,0) rot=(0,0,1;3.14159rad)
  Profile = -> Sketch131
  Type = 0
FEATURE [PartDesign::Pocket] Pocket041
  BaseFeature = -> Pad011
  Length = 0.6
  Length2 = 100
  Placement = pos=(0,0,0) rot=(0,0,1;3.14159rad)
  Profile = -> Sketch104
  Reversed = true
  Type = 0
FEATURE [PartDesign::Body] Body004  label="BodyN1"
  Group = -> [Sketch104,Sketch131,Pad011,Pocket041]
  Origin = -> Origin006
  Placement = pos=(0.75,0,0) rot=(0,0,1;0rad)
  Tip = -> Pocket041
FEATURE [PartDesign::Pad] Pad012
  Length = 0.65
  Length2 = 100
  Placement = pos=(0,0,0) rot=(0,0,1;3.14159rad)
  Profile = -> Sketch128
  Type = 0
FEATURE [PartDesign::Pocket] Pocket042
  BaseFeature = -> Pad012
  Length = 0.6
  Length2 = 100
  Placement = pos=(0,0,0) rot=(0,0,1;3.14159rad)
  Profile = -> Sketch105
  Reversed = true
  Type = 0
FEATURE [PartDesign::Body] Body005  label="BodyE1"
  Group = -> [Sketch105,Sketch128,Pad012,Pocket042]
  Origin = -> Origin007
  Placement = pos=(0.25,0,0) rot=(0,0,1;0rad)
  Tip = -> Pocket042
FEATURE [PartDesign::Pad] Pad013
  Length = 0.65
  Length2 = 100
  Placement = pos=(0,0,0) rot=(0,0,1;3.14159rad)
  Profile = -> Sketch135
  Type = 0
FEATURE [PartDesign::Pocket] Pocket043
  BaseFeature = -> Pad013
  Length = 0.6
  Length2 = 100
  Placement = pos=(0,0,0) rot=(0,0,1;3.14159rad)
  Profile = -> Sketch109
  Reversed = true
  Type = 0
FEATURE [PartDesign::Body] Body006  label="BodyR1"
  Group = -> [Sketch109,Sketch135,Pad013,Pocket043]
  Origin = -> Origin008
  Placement = pos=(-1,0,0) rot=(0,0,1;0rad)
  Tip = -> Pocket043
FEATURE [PartDesign::Pad] Pad014
  Length = 0.65
  Length2 = 100
  Placement = pos=(0,0,0) rot=(0,0,1;3.14159rad)
  Profile = -> Sketch134
  Type = 0
FEATURE [PartDesign::Pocket] Pocket044
  BaseFeature = -> Pad014
  Length = 0.6
  Length2 = 100
  Placement = pos=(0,0,0) rot=(0,0,1;3.14159rad)
  Profile = -> Sketch107
  Reversed = true
  Type = 0
FEATURE [PartDesign::Body] Body007  label="BodyO2"
  Group = -> [Sketch107,Sketch134,Pad014,Pocket044]
  Origin = -> Origin009
  Placement = pos=(-1.25,0,0) rot=(0,0,1;0rad)
  Tip = -> Pocket044
FEATURE [App::Part] Part001  label="FDMBlack"
  Group = -> [Body001,Body002,Body003,Body004,Body005,Body006,Body007]
  Origin = -> Origin002
FEATURE [Sketcher::SketchObject] Sketch136
  Placement = pos=(1.25,0,0) rot=(0,0,1;3.14159rad)
  sketch-geometry (13):
    g0: BSplineCurve PolesCount=4 KnotsCount=2 Degree=3 IsPeriodic=0
    g1: BSplineCurve PolesCount=2 KnotsCount=2 Degree=1 IsPeriodic=0
    g2: BSplineCurve PolesCount=2 KnotsCount=2 Degree=1 IsPeriodic=0
    g3: BSplineCurve PolesCount=2 KnotsCount=2 Degree=1 IsPeriodic=0
    g4: BSplineCurve PolesCount=2 KnotsCount=2 Degree=1 IsPeriodic=0
    g5: BSplineCurve PolesCount=2 KnotsCount=2 Degree=1 IsPeriodic=0
    g6: BSplineCurve PolesCount=2 KnotsCount=2 Degree=1 IsPeriodic=0
    g7: BSplineCurve PolesCount=2 KnotsCount=2 Degree=1 IsPeriodic=0
    g8: BSplineCurve PolesCount=2 KnotsCount=2 Degree=1 IsPeriodic=0
    g9: BSplineCurve PolesCount=2 KnotsCount=2 Degree=1 IsPeriodic=0
    g10: BSplineCurve PolesCount=2 KnotsCount=2 Degree=1 IsPeriodic=0
    g11: BSplineCurve PolesCount=2 KnotsCount=2 Degree=1 IsPeriodic=0
    g12: BSplineCurve PolesCount=2 KnotsCount=2 Degree=1 IsPeriodic=0
  constraints (13):
    c: Coincident(g0,g1)
    c: Coincident(g1,g2)
    c: Coincident(g2,g3)
    c: Coincident(g3,g4)
    c: Coincident(g4,g5)
    c: Coincident(g5,g6)
    c: Coincident(g6,g7)
    c: Coincident(g7,g8)
    c: Coincident(g8,g9)
    c: Coincident(g9,g10)
    c: Coincident(g10,g11)
    c: Coincident(g11,g12)
    c: Coincident(g12,g0)
FEATURE [PartDesign::Pocket] Pocket045  label="Pockmontxt-M1"
  BaseFeature = -> Pocket011
  Length = 0.5
  Length2 = 100
  Profile = -> Sketch136
  Reversed = true
  Type = 0
FEATURE [Sketcher::SketchObject] Sketch137
  Placement = pos=(1,0,0) rot=(0,0,1;3.14159rad)
  sketch-geometry (24):
    g0: BSplineCurve PolesCount=4 KnotsCount=2 Degree=3 IsPeriodic=0
    g1: BSplineCurve PolesCount=4 KnotsCount=2 Degree=3 IsPeriodic=0
    g2: BSplineCurve PolesCount=4 KnotsCount=2 Degree=3 IsPeriodic=0
    g3: BSplineCurve PolesCount=4 KnotsCount=2 Degree=3 IsPeriodic=0
    g4: BSplineCurve PolesCount=4 KnotsCount=2 Degree=3 IsPeriodic=0
    g5: BSplineCurve PolesCount=2 KnotsCount=2 Degree=1 IsPeriodic=0
    g6: BSplineCurve PolesCount=4 KnotsCount=2 Degree=3 IsPeriodic=0
    g7: BSplineCurve PolesCount=4 KnotsCount=2 Degree=3 IsPeriodic=0
    g8: BSplineCurve PolesCount=4 KnotsCount=2 Degree=3 IsPeriodic=0
    g9: BSplineCurve PolesCount=2 KnotsCount=2 Degree=1 IsPeriodic=0
    g10: BSplineCurve PolesCount=4 KnotsCount=2 Degree=3 IsPeriodic=0
    g11: BSplineCurve PolesCount=4 KnotsCount=2 Degree=3 IsPeriodic=0
    g12: BSplineCurve PolesCount=4 KnotsCount=2 Degree=3 IsPeriodic=0
    g13: BSplineCurve PolesCount=4 KnotsCount=2 Degree=3 IsPeriodic=0
    g14: BSplineCurve PolesCount=4 KnotsCount=2 Degree=3 IsPeriodic=0
    g15: BSplineCurve PolesCount=4 KnotsCount=2 Degree=3 IsPeriodic=0
    g16: BSplineCurve PolesCount=4 KnotsCount=2 Degree=3 IsPeriodic=0
    g17: BSplineCurve PolesCount=4 KnotsCount=2 Degree=3 IsPeriodic=0
    g18: BSplineCurve PolesCount=4 KnotsCount=2 Degree=3 IsPeriodic=0
    g19: BSplineCurve PolesCount=4 KnotsCount=2 Degree=3 IsPeriodic=0
    g20: BSplineCurve PolesCount=2 KnotsCount=2 Degree=1 IsPeriodic=0
    g21: BSplineCurve PolesCount=2 KnotsCount=2 Degree=1 IsPeriodic=0
    g22: BSplineCurve PolesCount=4 KnotsCount=2 Degree=3 IsPeriodic=0
    g23: BSplineCurve PolesCount=2 KnotsCount=2 Degree=1 IsPeriodic=0
  constraints (24):
    c: Coincident(g0,g1)
    c: Coincident(g1,g2)
    c: Coincident(g2,g3)
    c: Coincident(g3,g4)
    c: Coincident(g4,g5)
    c: Coincident(g5,g6)
    c: Coincident(g6,g7)
    c: Coincident(g7,g8)
    c: Coincident(g8,g9)
    c: Coincident(g9,g0)
    c: Coincident(g10,g11)
    c: Coincident(g11,g12)
    c: Coincident(g12,g13)
    c: Coincident(g13,g14)
    c: Coincident(g14,g15)
    c: Coincident(g15,g16)
    c: Coincident(g16,g17)
    c: Coincident(g17,g18)
    c: Coincident(g18,g19)
    c: Coincident(g19,g20)
    c: Coincident(g20,g21)
    c: Coincident(g21,g22)
    c: Coincident(g22,g23)
    c: Coincident(g23,g10)
FEATURE [PartDesign::Pocket] Pocket046  label="Pockmontxt-O1"
  BaseFeature = -> Pocket045
  Length = 0.5
  Length2 = 100
  Profile = -> Sketch137
  Reversed = true
  Type = 0
FEATURE [Sketcher::SketchObject] Sketch138
  Placement = pos=(0.75,0,0) rot=(0,0,1;3.14159rad)
  sketch-geometry (10):
    g0: BSplineCurve PolesCount=4 KnotsCount=2 Degree=3 IsPeriodic=0
    g1: BSplineCurve PolesCount=2 KnotsCount=2 Degree=1 IsPeriodic=0
    g2: BSplineCurve PolesCount=2 KnotsCount=2 Degree=1 IsPeriodic=0
    g3: BSplineCurve PolesCount=2 KnotsCount=2 Degree=1 IsPeriodic=0
    g4: BSplineCurve PolesCount=2 KnotsCount=2 Degree=1 IsPeriodic=0
    g5: BSplineCurve PolesCount=2 KnotsCount=2 Degree=1 IsPeriodic=0
    g6: BSplineCurve PolesCount=2 KnotsCount=2 Degree=1 IsPeriodic=0
    g7: BSplineCurve PolesCount=2 KnotsCount=2 Degree=1 IsPeriodic=0
    g8: BSplineCurve PolesCount=2 KnotsCount=2 Degree=1 IsPeriodic=0
    g9: BSplineCurve PolesCount=2 KnotsCount=2 Degree=1 IsPeriodic=0
  constraints (10):
    c: Coincident(g0,g1)
    c: Coincident(g1,g2)
    c: Coincident(g2,g3)
    c: Coincident(g3,g4)
    c: Coincident(g4,g5)
    c: Coincident(g5,g6)
    c: Coincident(g6,g7)
    c: Coincident(g7,g8)
    c: Coincident(g8,g9)
    c: Coincident(g9,g0)
FEATURE [PartDesign::Pocket] Pocket047  label="Pockmontxt-N1"
  BaseFeature = -> Pocket046
  Length = 0.5
  Length2 = 100
  Profile = -> Sketch138
  Reversed = true
  Type = 0
FEATURE [Sketcher::SketchObject] Sketch139
  Placement = pos=(0.25,0,0) rot=(0,0,1;3.14159rad)
  sketch-geometry (12):
    g0: BSplineCurve PolesCount=4 KnotsCount=2 Degree=3 IsPeriodic=0
    g1: BSplineCurve PolesCount=2 KnotsCount=2 Degree=1 IsPeriodic=0
    g2: BSplineCurve PolesCount=2 KnotsCount=2 Degree=1 IsPeriodic=0
    g3: BSplineCurve PolesCount=2 KnotsCount=2 Degree=1 IsPeriodic=0
    g4: BSplineCurve PolesCount=2 KnotsCount=2 Degree=1 IsPeriodic=0
    g5: BSplineCurve PolesCount=2 KnotsCount=2 Degree=1 IsPeriodic=0
    g6: BSplineCurve PolesCount=2 KnotsCount=2 Degree=1 IsPeriodic=0
    g7: BSplineCurve PolesCount=2 KnotsCount=2 Degree=1 IsPeriodic=0
    g8: BSplineCurve PolesCount=2 KnotsCount=2 Degree=1 IsPeriodic=0
    g9: BSplineCurve PolesCount=2 KnotsCount=2 Degree=1 IsPeriodic=0
    g10: BSplineCurve PolesCount=2 KnotsCount=2 Degree=1 IsPeriodic=0
    g11: BSplineCurve PolesCount=2 KnotsCount=2 Degree=1 IsPeriodic=0
  constraints (12):
    c: Coincident(g0,g1)
    c: Coincident(g1,g2)
    c: Coincident(g2,g3)
    c: Coincident(g3,g4)
    c: Coincident(g4,g5)
    c: Coincident(g5,g6)
    c: Coincident(g6,g7)
    c: Coincident(g7,g8)
    c: Coincident(g8,g9)
    c: Coincident(g9,g10)
    c: Coincident(g10,g11)
    c: Coincident(g11,g0)
FEATURE [PartDesign::Pocket] Pocket048  label="Pockmontxt-E1"
  BaseFeature = -> Pocket047
  Length = 0.5
  Length2 = 100
  Profile = -> Sketch139
  Reversed = true
  Type = 0
FEATURE [Sketcher::SketchObject] Sketch140
  Placement = pos=(-1,0,0) rot=(0,0,1;3.14159rad)
  sketch-geometry (29):
    g0: BSplineCurve PolesCount=2 KnotsCount=2 Degree=1 IsPeriodic=0
    g1: BSplineCurve PolesCount=4 KnotsCount=2 Degree=3 IsPeriodic=0
    g2: BSplineCurve PolesCount=2 KnotsCount=2 Degree=1 IsPeriodic=0
    g3: BSplineCurve PolesCount=2 KnotsCount=2 Degree=1 IsPeriodic=0
    g4: BSplineCurve PolesCount=2 KnotsCount=2 Degree=1 IsPeriodic=0
    g5: BSplineCurve PolesCount=2 KnotsCount=2 Degree=1 IsPeriodic=0
    g6: BSplineCurve PolesCount=2 KnotsCount=2 Degree=1 IsPeriodic=0
    g7: BSplineCurve PolesCount=2 KnotsCount=2 Degree=1 IsPeriodic=0
    g8: BSplineCurve PolesCount=4 KnotsCount=2 Degree=3 IsPeriodic=0
    g9: BSplineCurve PolesCount=4 KnotsCount=2 Degree=3 IsPeriodic=0
    g10: BSplineCurve PolesCount=4 KnotsCount=2 Degree=3 IsPeriodic=0
    g11: BSplineCurve PolesCount=2 KnotsCount=2 Degree=1 IsPeriodic=0
    g12: BSplineCurve PolesCount=2 KnotsCount=2 Degree=1 IsPeriodic=0
    g13: BSplineCurve PolesCount=4 KnotsCount=2 Degree=3 IsPeriodic=0
    g14: BSplineCurve PolesCount=2 KnotsCount=2 Degree=1 IsPeriodic=0
    g15: BSplineCurve PolesCount=2 KnotsCount=2 Degree=1 IsPeriodic=0
    g16: BSplineCurve PolesCount=4 KnotsCount=2 Degree=3 IsPeriodic=0
    g17: BSplineCurve PolesCount=2 KnotsCount=2 Degree=1 IsPeriodic=0
    g18: BSplineCurve PolesCount=2 KnotsCount=2 Degree=1 IsPeriodic=0
    g19: BSplineCurve PolesCount=4 KnotsCount=2 Degree=3 IsPeriodic=0
    g20: BSplineCurve PolesCount=4 KnotsCount=2 Degree=3 IsPeriodic=0
    g21: BSplineCurve PolesCount=4 KnotsCount=2 Degree=3 IsPeriodic=0
    g22: BSplineCurve PolesCount=4 KnotsCount=2 Degree=3 IsPeriodic=0
    g23: BSplineCurve PolesCount=4 KnotsCount=2 Degree=3 IsPeriodic=0
    g24: BSplineCurve PolesCount=2 KnotsCount=2 Degree=1 IsPeriodic=0
    g25: BSplineCurve PolesCount=2 KnotsCount=2 Degree=1 IsPeriodic=0
    g26: BSplineCurve PolesCount=4 KnotsCount=2 Degree=3 IsPeriodic=0
    g27: BSplineCurve PolesCount=2 KnotsCount=2 Degree=1 IsPeriodic=0
    g28: BSplineCurve PolesCount=2 KnotsCount=2 Degree=1 IsPeriodic=0
  constraints (29):
    c: Coincident(g0,g1)
    c: Coincident(g1,g2)
    c: Coincident(g2,g3)
    c: Coincident(g3,g4)
    c: Coincident(g4,g5)
    c: Coincident(g5,g6)
    c: Coincident(g6,g7)
    c: Coincident(g7,g8)
    c: Coincident(g8,g9)
    c: Coincident(g9,g10)
    c: Coincident(g10,g11)
    c: Coincident(g11,g12)
    c: Coincident(g12,g13)
    c: Coincident(g13,g14)
    c: Coincident(g14,g15)
    c: Coincident(g15,g16)
    c: Coincident(g16,g17)
    c: Coincident(g17,g0)
    c: Coincident(g18,g19)
    c: Coincident(g19,g20)
    c: Coincident(g20,g21)
    c: Coincident(g21,g22)
    c: Coincident(g22,g23)
    c: Coincident(g23,g24)
    c: Coincident(g24,g25)
    c: Coincident(g25,g26)
    c: Coincident(g26,g27)
    c: Coincident(g27,g28)
    c: Coincident(g28,g18)
FEATURE [PartDesign::Pocket] Pocket049  label="Pockmontxt-R1"
  BaseFeature = -> Pocket048
  Length = 0.5
  Length2 = 100
  Profile = -> Sketch140
  Reversed = true
  Type = 0
FEATURE [Sketcher::SketchObject] Sketch141
  Placement = pos=(-1.25,0,0) rot=(0,0,1;3.14159rad)
  sketch-geometry (25):
    g0: BSplineCurve PolesCount=4 KnotsCount=2 Degree=3 IsPeriodic=0
    g1: BSplineCurve PolesCount=4 KnotsCount=2 Degree=3 IsPeriodic=0
    g2: BSplineCurve PolesCount=4 KnotsCount=2 Degree=3 IsPeriodic=0
    g3: BSplineCurve PolesCount=4 KnotsCount=2 Degree=3 IsPeriodic=0
    g4: BSplineCurve PolesCount=4 KnotsCount=2 Degree=3 IsPeriodic=0
    g5: BSplineCurve PolesCount=4 KnotsCount=2 Degree=3 IsPeriodic=0
    g6: BSplineCurve PolesCount=4 KnotsCount=2 Degree=3 IsPeriodic=0
    g7: BSplineCurve PolesCount=4 KnotsCount=2 Degree=3 IsPeriodic=0
    g8: BSplineCurve PolesCount=4 KnotsCount=2 Degree=3 IsPeriodic=0
    g9: BSplineCurve PolesCount=4 KnotsCount=2 Degree=3 IsPeriodic=0
    g10: BSplineCurve PolesCount=2 KnotsCount=2 Degree=1 IsPeriodic=0
    g11: BSplineCurve PolesCount=2 KnotsCount=2 Degree=1 IsPeriodic=0
    g12: BSplineCurve PolesCount=4 KnotsCount=2 Degree=3 IsPeriodic=0
    g13: BSplineCurve PolesCount=2 KnotsCount=2 Degree=1 IsPeriodic=0
    g14: BSplineCurve PolesCount=4 KnotsCount=2 Degree=3 IsPeriodic=0
    g15: BSplineCurve PolesCount=4 KnotsCount=2 Degree=3 IsPeriodic=0
    g16: BSplineCurve PolesCount=4 KnotsCount=2 Degree=3 IsPeriodic=0
    g17: BSplineCurve PolesCount=4 KnotsCount=2 Degree=3 IsPeriodic=0
    g18: BSplineCurve PolesCount=4 KnotsCount=2 Degree=3 IsPeriodic=0
    g19: BSplineCurve PolesCount=2 KnotsCount=2 Degree=1 IsPeriodic=0
    g20: BSplineCurve PolesCount=2 KnotsCount=2 Degree=1 IsPeriodic=0
    g21: BSplineCurve PolesCount=4 KnotsCount=2 Degree=3 IsPeriodic=0
    g22: BSplineCurve PolesCount=4 KnotsCount=2 Degree=3 IsPeriodic=0
    g23: BSplineCurve PolesCount=4 KnotsCount=2 Degree=3 IsPeriodic=0
    g24: BSplineCurve PolesCount=2 KnotsCount=2 Degree=1 IsPeriodic=0
  constraints (25):
    c: Coincident(g0,g1)
    c: Coincident(g1,g2)
    c: Coincident(g2,g3)
    c: Coincident(g3,g4)
    c: Coincident(g4,g5)
    c: Coincident(g5,g6)
    c: Coincident(g6,g7)
    c: Coincident(g7,g8)
    c: Coincident(g8,g9)
    c: Coincident(g9,g10)
    c: Coincident(g10,g11)
    c: Coincident(g11,g12)
    c: Coincident(g12,g13)
    c: Coincident(g13,g0)
    c: Coincident(g14,g15)
    c: Coincident(g15,g16)
    c: Coincident(g16,g17)
    c: Coincident(g17,g18)
    c: Coincident(g18,g19)
    c: Coincident(g19,g20)
    c: Coincident(g20,g21)
    c: Coincident(g21,g22)
    c: Coincident(g22,g23)
    c: Coincident(g23,g24)
    c: Coincident(g24,g14)
FEATURE [PartDesign::Pocket] Pocket050  label="Pockmontxt-O2"
  BaseFeature = -> Pocket049
  Length = 0.65
  Length2 = 100
  Profile = -> Sketch141
  Reversed = true
  Type = 0
FEATURE [Sketcher::SketchObject] Sketch142
  Placement = pos=(1,0,0) rot=(0,0,1;3.14159rad)
  sketch-geometry (13):
    g0: BSplineCurve PolesCount=2 KnotsCount=2 Degree=1 IsPeriodic=0
    g1: BSplineCurve PolesCount=2 KnotsCount=2 Degree=1 IsPeriodic=0
    g2: BSplineCurve PolesCount=2 KnotsCount=2 Degree=1 IsPeriodic=0
    g3: BSplineCurve PolesCount=2 KnotsCount=2 Degree=1 IsPeriodic=0
    g4: BSplineCurve PolesCount=2 KnotsCount=2 Degree=1 IsPeriodic=0
    g5: BSplineCurve PolesCount=2 KnotsCount=2 Degree=1 IsPeriodic=0
    g6: BSplineCurve PolesCount=2 KnotsCount=2 Degree=1 IsPeriodic=0
    g7: BSplineCurve PolesCount=2 KnotsCount=2 Degree=1 IsPeriodic=0
    g8: BSplineCurve PolesCount=2 KnotsCount=2 Degree=1 IsPeriodic=0
    g9: BSplineCurve PolesCount=2 KnotsCount=2 Degree=1 IsPeriodic=0
    g10: BSplineCurve PolesCount=2 KnotsCount=2 Degree=1 IsPeriodic=0
    g11: BSplineCurve PolesCount=2 KnotsCount=2 Degree=1 IsPeriodic=0
    g12: BSplineCurve PolesCount=2 KnotsCount=2 Degree=1 IsPeriodic=0
  constraints (13):
    c: Coincident(g0,g1)
    c: Coincident(g1,g2)
    c: Coincident(g2,g3)
    c: Coincident(g3,g4)
    c: Coincident(g4,g5)
    c: Coincident(g5,g6)
    c: Coincident(g6,g7)
    c: Coincident(g7,g8)
    c: Coincident(g8,g9)
    c: Coincident(g9,g10)
    c: Coincident(g10,g11)
    c: Coincident(g11,g12)
    c: Coincident(g12,g0)
FEATURE [PartDesign::Pad] Pad015
  Length = 0.6
  Length2 = 100
  Placement = pos=(1,0,0) rot=(0,0,1;3.14159rad)
  Profile = -> Sketch142
  Type = 0
FEATURE [PartDesign::Body] Body008  label="BodyMa"
  Group = -> [Sketch142,Pad015]
  Origin = -> Origin011
  Placement = pos=(0.25,0,0) rot=(0,0,1;0rad)
  Tip = -> Pad015
FEATURE [Sketcher::SketchObject] Sketch143
  Placement = pos=(1,0,0) rot=(0,0,1;3.14159rad)
  sketch-geometry (17):
    g0: BSplineCurve PolesCount=4 KnotsCount=2 Degree=3 IsPeriodic=0
    g1: BSplineCurve PolesCount=4 KnotsCount=2 Degree=3 IsPeriodic=0
    g2: BSplineCurve PolesCount=4 KnotsCount=2 Degree=3 IsPeriodic=0
    g3: BSplineCurve PolesCount=4 KnotsCount=2 Degree=3 IsPeriodic=0
    g4: BSplineCurve PolesCount=4 KnotsCount=2 Degree=3 IsPeriodic=0
    g5: BSplineCurve PolesCount=4 KnotsCount=2 Degree=3 IsPeriodic=0
    g6: BSplineCurve PolesCount=4 KnotsCount=2 Degree=3 IsPeriodic=0
    g7: BSplineCurve PolesCount=4 KnotsCount=2 Degree=3 IsPeriodic=0
    g8: BSplineCurve PolesCount=4 KnotsCount=2 Degree=3 IsPeriodic=0
    g9: BSplineCurve PolesCount=4 KnotsCount=2 Degree=3 IsPeriodic=0
    g10: BSplineCurve PolesCount=4 KnotsCount=2 Degree=3 IsPeriodic=0
    g11: BSplineCurve PolesCount=4 KnotsCount=2 Degree=3 IsPeriodic=0
    g12: BSplineCurve PolesCount=4 KnotsCount=2 Degree=3 IsPeriodic=0
    g13: BSplineCurve PolesCount=4 KnotsCount=2 Degree=3 IsPeriodic=0
    g14: BSplineCurve PolesCount=4 KnotsCount=2 Degree=3 IsPeriodic=0
    g15: BSplineCurve PolesCount=4 KnotsCount=2 Degree=3 IsPeriodic=0
    g16: BSplineCurve PolesCount=4 KnotsCount=2 Degree=3 IsPeriodic=0
  constraints (17):
    c: Coincident(g0,g1)
    c: Coincident(g1,g2)
    c: Coincident(g2,g3)
    c: Coincident(g3,g4)
    c: Coincident(g4,g5)
    c: Coincident(g5,g6)
    c: Coincident(g6,g7)
    c: Coincident(g7,g0)
    c: Coincident(g8,g9)
    c: Coincident(g9,g10)
    c: Coincident(g10,g11)
    c: Coincident(g11,g12)
    c: Coincident(g12,g13)
    c: Coincident(g13,g14)
    c: Coincident(g14,g15)
    c: Coincident(g15,g16)
    c: Coincident(g16,g8)
FEATURE [PartDesign::Pad] Pad016
  Length = 0.6
  Length2 = 100
  Placement = pos=(1,0,0) rot=(0,0,1;3.14159rad)
  Profile = -> Sketch143
  Type = 0
FEATURE [PartDesign::Body] Body009  label="BodyOa"
  Group = -> [Sketch143,Pad016]
  Origin = -> Origin012
  Tip = -> Pad016
FEATURE [Sketcher::SketchObject] Sketch144
  Placement = pos=(0.75,0,0) rot=(0,0,1;3.14159rad)
  sketch-geometry (10):
    g0: BSplineCurve PolesCount=2 KnotsCount=2 Degree=1 IsPeriodic=0
    g1: BSplineCurve PolesCount=2 KnotsCount=2 Degree=1 IsPeriodic=0
    g2: BSplineCurve PolesCount=2 KnotsCount=2 Degree=1 IsPeriodic=0
    g3: BSplineCurve PolesCount=2 KnotsCount=2 Degree=1 IsPeriodic=0
    g4: BSplineCurve PolesCount=2 KnotsCount=2 Degree=1 IsPeriodic=0
    g5: BSplineCurve PolesCount=2 KnotsCount=2 Degree=1 IsPeriodic=0
    g6: BSplineCurve PolesCount=2 KnotsCount=2 Degree=1 IsPeriodic=0
    g7: BSplineCurve PolesCount=2 KnotsCount=2 Degree=1 IsPeriodic=0
    g8: BSplineCurve PolesCount=2 KnotsCount=2 Degree=1 IsPeriodic=0
    g9: BSplineCurve PolesCount=2 KnotsCount=2 Degree=1 IsPeriodic=0
  constraints (10):
    c: Coincident(g0,g1)
    c: Coincident(g1,g2)
    c: Coincident(g2,g3)
    c: Coincident(g3,g4)
    c: Coincident(g4,g5)
    c: Coincident(g5,g6)
    c: Coincident(g6,g7)
    c: Coincident(g7,g8)
    c: Coincident(g8,g9)
    c: Coincident(g9,g0)
FEATURE [PartDesign::Pad] Pad017
  Length = 0.6
  Length2 = 100
  Placement = pos=(0.75,0,0) rot=(0,0,1;3.14159rad)
  Profile = -> Sketch144
  Type = 0
FEATURE [PartDesign::Body] Body010  label="BodyNa"
  Group = -> [Sketch144,Pad017]
  Origin = -> Origin013
  Tip = -> Pad017
FEATURE [Sketcher::SketchObject] Sketch145
  Placement = pos=(0.25,0,0) rot=(0,0,1;3.14159rad)
  sketch-geometry (12):
    g0: BSplineCurve PolesCount=2 KnotsCount=2 Degree=1 IsPeriodic=0
    g1: BSplineCurve PolesCount=2 KnotsCount=2 Degree=1 IsPeriodic=0
    g2: BSplineCurve PolesCount=2 KnotsCount=2 Degree=1 IsPeriodic=0
    g3: BSplineCurve PolesCount=2 KnotsCount=2 Degree=1 IsPeriodic=0
    g4: BSplineCurve PolesCount=2 KnotsCount=2 Degree=1 IsPeriodic=0
    g5: BSplineCurve PolesCount=2 KnotsCount=2 Degree=1 IsPeriodic=0
    g6: BSplineCurve PolesCount=2 KnotsCount=2 Degree=1 IsPeriodic=0
    g7: BSplineCurve PolesCount=2 KnotsCount=2 Degree=1 IsPeriodic=0
    g8: BSplineCurve PolesCount=2 KnotsCount=2 Degree=1 IsPeriodic=0
    g9: BSplineCurve PolesCount=2 KnotsCount=2 Degree=1 IsPeriodic=0
    g10: BSplineCurve PolesCount=2 KnotsCount=2 Degree=1 IsPeriodic=0
    g11: BSplineCurve PolesCount=2 KnotsCount=2 Degree=1 IsPeriodic=0
  constraints (12):
    c: Coincident(g0,g1)
    c: Coincident(g1,g2)
    c: Coincident(g2,g3)
    c: Coincident(g3,g4)
    c: Coincident(g4,g5)
    c: Coincident(g5,g6)
    c: Coincident(g6,g7)
    c: Coincident(g7,g8)
    c: Coincident(g8,g9)
    c: Coincident(g9,g10)
    c: Coincident(g10,g11)
    c: Coincident(g11,g0)
FEATURE [PartDesign::Pad] Pad018
  Length = 0.6
  Length2 = 100
  Placement = pos=(0.25,0,0) rot=(0,0,1;3.14159rad)
  Profile = -> Sketch145
  Type = 0
FEATURE [PartDesign::Body] Body011  label="BodyEa"
  Group = -> [Sketch145,Pad018]
  Origin = -> Origin014
  Tip = -> Pad018
FEATURE [Sketcher::SketchObject] Sketch146
  Placement = pos=(-1,0,0) rot=(0,0,1;3.14159rad)
  sketch-geometry (21):
    g0: BSplineCurve PolesCount=2 KnotsCount=2 Degree=1 IsPeriodic=0
    g1: BSplineCurve PolesCount=2 KnotsCount=2 Degree=1 IsPeriodic=0
    g2: BSplineCurve PolesCount=4 KnotsCount=2 Degree=3 IsPeriodic=0
    g3: BSplineCurve PolesCount=4 KnotsCount=2 Degree=3 IsPeriodic=0
    g4: BSplineCurve PolesCount=4 KnotsCount=2 Degree=3 IsPeriodic=0
    g5: BSplineCurve PolesCount=4 KnotsCount=2 Degree=3 IsPeriodic=0
    g6: BSplineCurve PolesCount=4 KnotsCount=2 Degree=3 IsPeriodic=0
    g7: BSplineCurve PolesCount=2 KnotsCount=2 Degree=1 IsPeriodic=0
    g8: BSplineCurve PolesCount=2 KnotsCount=2 Degree=1 IsPeriodic=0
    g9: BSplineCurve PolesCount=2 KnotsCount=2 Degree=1 IsPeriodic=0
    g10: BSplineCurve PolesCount=2 KnotsCount=2 Degree=1 IsPeriodic=0
    g11: BSplineCurve PolesCount=2 KnotsCount=2 Degree=1 IsPeriodic=0
    g12: BSplineCurve PolesCount=2 KnotsCount=2 Degree=1 IsPeriodic=0
    g13: BSplineCurve PolesCount=2 KnotsCount=2 Degree=1 IsPeriodic=0
    g14: BSplineCurve PolesCount=2 KnotsCount=2 Degree=1 IsPeriodic=0
    g15: BSplineCurve PolesCount=4 KnotsCount=2 Degree=3 IsPeriodic=0
    g16: BSplineCurve PolesCount=4 KnotsCount=2 Degree=3 IsPeriodic=0
    g17: BSplineCurve PolesCount=4 KnotsCount=2 Degree=3 IsPeriodic=0
    g18: BSplineCurve PolesCount=4 KnotsCount=2 Degree=3 IsPeriodic=0
    g19: BSplineCurve PolesCount=4 KnotsCount=2 Degree=3 IsPeriodic=0
    g20: BSplineCurve PolesCount=2 KnotsCount=2 Degree=1 IsPeriodic=0
  constraints (21):
    c: Coincident(g0,g1)
    c: Coincident(g1,g2)
    c: Coincident(g2,g3)
    c: Coincident(g3,g4)
    c: Coincident(g4,g5)
    c: Coincident(g5,g6)
    c: Coincident(g6,g7)
    c: Coincident(g7,g0)
    c: Coincident(g8,g9)
    c: Coincident(g9,g10)
    c: Coincident(g10,g11)
    c: Coincident(g11,g12)
    c: Coincident(g12,g13)
    c: Coincident(g13,g14)
    c: Coincident(g14,g15)
    c: Coincident(g15,g16)
    c: Coincident(g16,g17)
    c: Coincident(g17,g18)
    c: Coincident(g18,g19)
    c: Coincident(g19,g20)
    c: Coincident(g20,g8)
FEATURE [PartDesign::Pad] Pad019
  Length = 0.6
  Length2 = 100
  Placement = pos=(-1,0,0) rot=(0,0,1;3.14159rad)
  Profile = -> Sketch146
  Type = 0
FEATURE [PartDesign::Body] Body012  label="BodyRa"
  Group = -> [Sketch146,Pad019]
  Origin = -> Origin015
  Tip = -> Pad019
FEATURE [Sketcher::SketchObject] Sketch147
  Placement = pos=(-1,0,0) rot=(0,0,1;3.14159rad)
  sketch-geometry (17):
    g0: BSplineCurve PolesCount=4 KnotsCount=2 Degree=3 IsPeriodic=0
    g1: BSplineCurve PolesCount=4 KnotsCount=2 Degree=3 IsPeriodic=0
    g2: BSplineCurve PolesCount=4 KnotsCount=2 Degree=3 IsPeriodic=0
    g3: BSplineCurve PolesCount=4 KnotsCount=2 Degree=3 IsPeriodic=0
    g4: BSplineCurve PolesCount=4 KnotsCount=2 Degree=3 IsPeriodic=0
    g5: BSplineCurve PolesCount=4 KnotsCount=2 Degree=3 IsPeriodic=0
    g6: BSplineCurve PolesCount=4 KnotsCount=2 Degree=3 IsPeriodic=0
    g7: BSplineCurve PolesCount=4 KnotsCount=2 Degree=3 IsPeriodic=0
    g8: BSplineCurve PolesCount=4 KnotsCount=2 Degree=3 IsPeriodic=0
    g9: BSplineCurve PolesCount=4 KnotsCount=2 Degree=3 IsPeriodic=0
    g10: BSplineCurve PolesCount=4 KnotsCount=2 Degree=3 IsPeriodic=0
    g11: BSplineCurve PolesCount=4 KnotsCount=2 Degree=3 IsPeriodic=0
    g12: BSplineCurve PolesCount=4 KnotsCount=2 Degree=3 IsPeriodic=0
    g13: BSplineCurve PolesCount=4 KnotsCount=2 Degree=3 IsPeriodic=0
    g14: BSplineCurve PolesCount=4 KnotsCount=2 Degree=3 IsPeriodic=0
    g15: BSplineCurve PolesCount=4 KnotsCount=2 Degree=3 IsPeriodic=0
    g16: BSplineCurve PolesCount=4 KnotsCount=2 Degree=3 IsPeriodic=0
  constraints (17):
    c: Coincident(g0,g1)
    c: Coincident(g1,g2)
    c: Coincident(g2,g3)
    c: Coincident(g3,g4)
    c: Coincident(g4,g5)
    c: Coincident(g5,g6)
    c: Coincident(g6,g7)
    c: Coincident(g7,g0)
    c: Coincident(g8,g9)
    c: Coincident(g9,g10)
    c: Coincident(g10,g11)
    c: Coincident(g11,g12)
    c: Coincident(g12,g13)
    c: Coincident(g13,g14)
    c: Coincident(g14,g15)
    c: Coincident(g15,g16)
    c: Coincident(g16,g8)
FEATURE [PartDesign::Pad] Pad020
  Length = 0.6
  Length2 = 100
  Placement = pos=(-1,0,0) rot=(0,0,1;3.14159rad)
  Profile = -> Sketch147
  Type = 0
FEATURE [PartDesign::Body] Body013  label="BodyOb"
  Group = -> [Sketch147,Pad020]
  Origin = -> Origin016
  Placement = pos=(-0.25,0,0) rot=(0,0,1;0rad)
  Tip = -> Pad020
FEATURE [App::Part] Part002  label="FDMOrange"
  Group = -> [Body008,Body009,Body010,Body011,Body012,Body013]
  Origin = -> Origin010
FEATURE [Sketcher::SketchObject] Sketch162  label="Resinidsymbol"
  Placement = pos=(-156,148,1.5) rot=(0,0,1;0rad)
  expr: Placement.Base.z = Spreadsheet.floorthick
  sketch-geometry (155):
    g0: BSplineCurve PolesCount=2 KnotsCount=2 Degree=1 IsPeriodic=0
    g1: BSplineCurve PolesCount=2 KnotsCount=2 Degree=1 IsPeriodic=0
    g2: BSplineCurve PolesCount=2 KnotsCount=2 Degree=1 IsPeriodic=0
    g3: BSplineCurve PolesCount=4 KnotsCount=2 Degree=3 IsPeriodic=0
    g4: BSplineCurve PolesCount=4 KnotsCount=2 Degree=3 IsPeriodic=0
    g5: BSplineCurve PolesCount=2 KnotsCount=2 Degree=1 IsPeriodic=0
    g6: BSplineCurve PolesCount=2 KnotsCount=2 Degree=1 IsPeriodic=0
    g7: BSplineCurve PolesCount=2 KnotsCount=2 Degree=1 IsPeriodic=0
    g8: BSplineCurve PolesCount=2 KnotsCount=2 Degree=1 IsPeriodic=0
    g9: BSplineCurve PolesCount=2 KnotsCount=2 Degree=1 IsPeriodic=0
    g10: BSplineCurve PolesCount=2 KnotsCount=2 Degree=1 IsPeriodic=0
    g11: BSplineCurve PolesCount=4 KnotsCount=2 Degree=3 IsPeriodic=0
    g12: BSplineCurve PolesCount=4 KnotsCount=2 Degree=3 IsPeriodic=0
    g13: BSplineCurve PolesCount=3 KnotsCount=2 Degree=2 IsPeriodic=0
    g14: BSplineCurve PolesCount=3 KnotsCount=2 Degree=2 IsPeriodic=0
    g15: BSplineCurve PolesCount=2 KnotsCount=2 Degree=1 IsPeriodic=0
    g16: BSplineCurve PolesCount=2 KnotsCount=2 Degree=1 IsPeriodic=0
    g17: BSplineCurve PolesCount=2 KnotsCount=2 Degree=1 IsPeriodic=0
    g18: BSplineCurve PolesCount=3 KnotsCount=2 Degree=2 IsPeriodic=0
    g19: BSplineCurve PolesCount=3 KnotsCount=2 Degree=2 IsPeriodic=0
    g20: BSplineCurve PolesCount=3 KnotsCount=2 Degree=2 IsPeriodic=0
    g21: BSplineCurve PolesCount=3 KnotsCount=2 Degree=2 IsPeriodic=0
    g22: BSplineCurve PolesCount=3 KnotsCount=2 Degree=2 IsPeriodic=0
    g23: BSplineCurve PolesCount=3 KnotsCount=2 Degree=2 IsPeriodic=0
    g24: BSplineCurve PolesCount=3 KnotsCount=2 Degree=2 IsPeriodic=0
    g25: BSplineCurve PolesCount=3 KnotsCount=2 Degree=2 IsPeriodic=0
    g26: BSplineCurve PolesCount=3 KnotsCount=2 Degree=2 IsPeriodic=0
    g27: BSplineCurve PolesCount=3 KnotsCount=2 Degree=2 IsPeriodic=0
    g28: BSplineCurve PolesCount=2 KnotsCount=2 Degree=1 IsPeriodic=0
    g29: BSplineCurve PolesCount=3 KnotsCount=2 Degree=2 IsPeriodic=0
    g30: BSplineCurve PolesCount=3 KnotsCount=2 Degree=2 IsPeriodic=0
    g31: BSplineCurve PolesCount=3 KnotsCount=2 Degree=2 IsPeriodic=0
    g32: BSplineCurve PolesCount=3 KnotsCount=2 Degree=2 IsPeriodic=0
    g33: BSplineCurve PolesCount=3 KnotsCount=2 Degree=2 IsPeriodic=0
    g34: BSplineCurve PolesCount=3 KnotsCount=2 Degree=2 IsPeriodic=0
    g35: BSplineCurve PolesCount=3 KnotsCount=2 Degree=2 IsPeriodic=0
    g36: BSplineCurve PolesCount=3 KnotsCount=2 Degree=2 IsPeriodic=0
    g37: BSplineCurve PolesCount=3 KnotsCount=2 Degree=2 IsPeriodic=0
    g38: BSplineCurve PolesCount=3 KnotsCount=2 Degree=2 IsPeriodic=0
    g39: BSplineCurve PolesCount=3 KnotsCount=2 Degree=2 IsPeriodic=0
    g40: BSplineCurve PolesCount=3 KnotsCount=2 Degree=2 IsPeriodic=0
    g41: BSplineCurve PolesCount=3 KnotsCount=2 Degree=2 IsPeriodic=0
    g42: BSplineCurve PolesCount=3 KnotsCount=2 Degree=2 IsPeriodic=0
    g43: BSplineCurve PolesCount=2 KnotsCount=2 Degree=1 IsPeriodic=0
    g44: BSplineCurve PolesCount=3 KnotsCount=2 Degree=2 IsPeriodic=0
    g45: BSplineCurve PolesCount=3 KnotsCount=2 Degree=2 IsPeriodic=0
    g46: BSplineCurve PolesCount=3 KnotsCount=2 Degree=2 IsPeriodic=0
    g47: BSplineCurve PolesCount=3 KnotsCount=2 Degree=2 IsPeriodic=0
    g48: BSplineCurve PolesCount=3 KnotsCount=2 Degree=2 IsPeriodic=0
    g49: BSplineCurve PolesCount=3 KnotsCount=2 Degree=2 IsPeriodic=0
    g50: BSplineCurve PolesCount=3 KnotsCount=2 Degree=2 IsPeriodic=0
    g51: BSplineCurve PolesCount=3 KnotsCount=2 Degree=2 IsPeriodic=0
    g52: BSplineCurve PolesCount=3 KnotsCount=2 Degree=2 IsPeriodic=0
    g53: BSplineCurve PolesCount=2 KnotsCount=2 Degree=1 IsPeriodic=0
    g54: BSplineCurve PolesCount=2 KnotsCount=2 Degree=1 IsPeriodic=0
    g55: BSplineCurve PolesCount=2 KnotsCount=2 Degree=1 IsPeriodic=0
    g56: BSplineCurve PolesCount=4 KnotsCount=2 Degree=3 IsPeriodic=0
    g57: BSplineCurve PolesCount=4 KnotsCount=2 Degree=3 IsPeriodic=0
    g58: BSplineCurve PolesCount=2 KnotsCount=2 Degree=1 IsPeriodic=0
    g59: BSplineCurve PolesCount=2 KnotsCount=2 Degree=1 IsPeriodic=0
    g60: BSplineCurve PolesCount=2 KnotsCount=2 Degree=1 IsPeriodic=0
    g61: BSplineCurve PolesCount=2 KnotsCount=2 Degree=1 IsPeriodic=0
    g62: BSplineCurve PolesCount=2 KnotsCount=2 Degree=1 IsPeriodic=0
    g63: BSplineCurve PolesCount=2 KnotsCount=2 Degree=1 IsPeriodic=0
    g64: BSplineCurve PolesCount=4 KnotsCount=2 Degree=3 IsPeriodic=0
    g65: BSplineCurve PolesCount=4 KnotsCount=2 Degree=3 IsPeriodic=0
    g66: BSplineCurve PolesCount=3 KnotsCount=2 Degree=2 IsPeriodic=0
    g67: BSplineCurve PolesCount=3 KnotsCount=2 Degree=2 IsPeriodic=0
    g68: BSplineCurve PolesCount=2 KnotsCount=2 Degree=1 IsPeriodic=0
    g69: BSplineCurve PolesCount=2 KnotsCount=2 Degree=1 IsPeriodic=0
    g70: BSplineCurve PolesCount=2 KnotsCount=2 Degree=1 IsPeriodic=0
    g71: BSplineCurve PolesCount=3 KnotsCount=2 Degree=2 IsPeriodic=0
    g72: BSplineCurve PolesCount=3 KnotsCount=2 Degree=2 IsPeriodic=0
    g73: BSplineCurve PolesCount=3 KnotsCount=2 Degree=2 IsPeriodic=0
    g74: BSplineCurve PolesCount=2 KnotsCount=2 Degree=1 IsPeriodic=0
    g75: BSplineCurve PolesCount=2 KnotsCount=2 Degree=1 IsPeriodic=0
    g76: BSplineCurve PolesCount=2 KnotsCount=2 Degree=1 IsPeriodic=0
    g77: BSplineCurve PolesCount=3 KnotsCount=2 Degree=2 IsPeriodic=0
    g78: BSplineCurve PolesCount=3 KnotsCount=2 Degree=2 IsPeriodic=0
    g79: BSplineCurve PolesCount=2 KnotsCount=2 Degree=1 IsPeriodic=0
    g80: BSplineCurve PolesCount=2 KnotsCount=2 Degree=1 IsPeriodic=0
    g81: BSplineCurve PolesCount=2 KnotsCount=2 Degree=1 IsPeriodic=0
    g82: BSplineCurve PolesCount=2 KnotsCount=2 Degree=1 IsPeriodic=0
    g83: BSplineCurve PolesCount=2 KnotsCount=2 Degree=1 IsPeriodic=0
    g84: BSplineCurve PolesCount=2 KnotsCount=2 Degree=1 IsPeriodic=0
    g85: BSplineCurve PolesCount=2 KnotsCount=2 Degree=1 IsPeriodic=0
    g86: BSplineCurve PolesCount=2 KnotsCount=2 Degree=1 IsPeriodic=0
    g87: BSplineCurve PolesCount=2 KnotsCount=2 Degree=1 IsPeriodic=0
    g88: BSplineCurve PolesCount=2 KnotsCount=2 Degree=1 IsPeriodic=0
    g89: BSplineCurve PolesCount=2 KnotsCount=2 Degree=1 IsPeriodic=0
    g90: BSplineCurve PolesCount=2 KnotsCount=2 Degree=1 IsPeriodic=0
    g91: BSplineCurve PolesCount=3 KnotsCount=2 Degree=2 IsPeriodic=0
    g92: BSplineCurve PolesCount=3 KnotsCount=2 Degree=2 IsPeriodic=0
    g93: BSplineCurve PolesCount=3 KnotsCount=2 Degree=2 IsPeriodic=0
    g94: BSplineCurve PolesCount=2 KnotsCount=2 Degree=1 IsPeriodic=0
    g95: BSplineCurve PolesCount=3 KnotsCount=2 Degree=2 IsPeriodic=0
    g96: BSplineCurve PolesCount=3 KnotsCount=2 Degree=2 IsPeriodic=0
    g97: BSplineCurve PolesCount=3 KnotsCount=2 Degree=2 IsPeriodic=0
    g98: BSplineCurve PolesCount=3 KnotsCount=2 Degree=2 IsPeriodic=0
    g99: BSplineCurve PolesCount=3 KnotsCount=2 Degree=2 IsPeriodic=0
    g100: BSplineCurve PolesCount=3 KnotsCount=2 Degree=2 IsPeriodic=0
    g101: BSplineCurve PolesCount=2 KnotsCount=2 Degree=1 IsPeriodic=0
    g102: BSplineCurve PolesCount=3 KnotsCount=2 Degree=2 IsPeriodic=0
    g103: BSplineCurve PolesCount=3 KnotsCount=2 Degree=2 IsPeriodic=0
    g104: BSplineCurve PolesCount=3 KnotsCount=2 Degree=2 IsPeriodic=0
    g105: BSplineCurve PolesCount=2 KnotsCount=2 Degree=1 IsPeriodic=0
    g106: BSplineCurve PolesCount=2 KnotsCount=2 Degree=1 IsPeriodic=0
    g107: BSplineCurve PolesCount=2 KnotsCount=2 Degree=1 IsPeriodic=0
    g108: BSplineCurve PolesCount=2 KnotsCount=2 Degree=1 IsPeriodic=0
    g109: BSplineCurve PolesCount=2 KnotsCount=2 Degree=1 IsPeriodic=0
    g110: BSplineCurve PolesCount=2 KnotsCount=2 Degree=1 IsPeriodic=0
    g111: BSplineCurve PolesCount=2 KnotsCount=2 Degree=1 IsPeriodic=0
    g112: BSplineCurve PolesCount=2 KnotsCount=2 Degree=1 IsPeriodic=0
    g113: BSplineCurve PolesCount=3 KnotsCount=2 Degree=2 IsPeriodic=0
    g114: BSplineCurve PolesCount=3 KnotsCount=2 Degree=2 IsPeriodic=0
    g115: BSplineCurve PolesCount=3 KnotsCount=2 Degree=2 IsPeriodic=0
    g116: BSplineCurve PolesCount=2 KnotsCount=2 Degree=1 IsPeriodic=0
    g117: BSplineCurve PolesCount=2 KnotsCount=2 Degree=1 IsPeriodic=0
    g118: BSplineCurve PolesCount=2 KnotsCount=2 Degree=1 IsPeriodic=0
    g119: BSplineCurve PolesCount=2 KnotsCount=2 Degree=1 IsPeriodic=0
    g120: BSplineCurve PolesCount=2 KnotsCount=2 Degree=1 IsPeriodic=0
    g121: BSplineCurve PolesCount=3 KnotsCount=2 Degree=2 IsPeriodic=0
    g122: BSplineCurve PolesCount=3 KnotsCount=2 Degree=2 IsPeriodic=0
    g123: BSplineCurve PolesCount=3 KnotsCount=2 Degree=2 IsPeriodic=0
    g124: BSplineCurve PolesCount=3 KnotsCount=2 Degree=2 IsPeriodic=0
    g125: BSplineCurve PolesCount=2 KnotsCount=2 Degree=1 IsPeriodic=0
    g126: BSplineCurve PolesCount=3 KnotsCount=2 Degree=2 IsPeriodic=0
    g127: BSplineCurve PolesCount=3 KnotsCount=2 Degree=2 IsPeriodic=0
    g128: BSplineCurve PolesCount=3 KnotsCount=2 Degree=2 IsPeriodic=0
    g129: BSplineCurve PolesCount=2 KnotsCount=2 Degree=1 IsPeriodic=0
    g130: BSplineCurve PolesCount=2 KnotsCount=2 Degree=1 IsPeriodic=0
    g131: BSplineCurve PolesCount=2 KnotsCount=2 Degree=1 IsPeriodic=0
    g132: BSplineCurve PolesCount=3 KnotsCount=2 Degree=2 IsPeriodic=0
    g133: BSplineCurve PolesCount=2 KnotsCount=2 Degree=1 IsPeriodic=0
    g134: BSplineCurve PolesCount=2 KnotsCount=2 Degree=1 IsPeriodic=0
    g135: BSplineCurve PolesCount=2 KnotsCount=2 Degree=1 IsPeriodic=0
    g136: BSplineCurve PolesCount=4 KnotsCount=2 Degree=3 IsPeriodic=0
    g137: BSplineCurve PolesCount=4 KnotsCount=2 Degree=3 IsPeriodic=0
    g138: BSplineCurve PolesCount=2 KnotsCount=2 Degree=1 IsPeriodic=0
    g139: BSplineCurve PolesCount=2 KnotsCount=2 Degree=1 IsPeriodic=0
    g140: BSplineCurve PolesCount=2 KnotsCount=2 Degree=1 IsPeriodic=0
    g141: BSplineCurve PolesCount=2 KnotsCount=2 Degree=1 IsPeriodic=0
    g142: BSplineCurve PolesCount=2 KnotsCount=2 Degree=1 IsPeriodic=0
    g143: BSplineCurve PolesCount=2 KnotsCount=2 Degree=1 IsPeriodic=0
    g144: BSplineCurve PolesCount=4 KnotsCount=2 Degree=3 IsPeriodic=0
    g145: BSplineCurve PolesCount=4 KnotsCount=2 Degree=3 IsPeriodic=0
    g146: BSplineCurve PolesCount=2 KnotsCount=2 Degree=1 IsPeriodic=0
    g147: BSplineCurve PolesCount=2 KnotsCount=2 Degree=1 IsPeriodic=0
    g148: BSplineCurve PolesCount=2 KnotsCount=2 Degree=1 IsPeriodic=0
    g149: BSplineCurve PolesCount=2 KnotsCount=2 Degree=1 IsPeriodic=0
    g150: BSplineCurve PolesCount=2 KnotsCount=2 Degree=1 IsPeriodic=0
    g151: BSplineCurve PolesCount=2 KnotsCount=2 Degree=1 IsPeriodic=0
    g152: BSplineCurve PolesCount=2 KnotsCount=2 Degree=1 IsPeriodic=0
    g153: BSplineCurve PolesCount=2 KnotsCount=2 Degree=1 IsPeriodic=0
    g154: BSplineCurve PolesCount=2 KnotsCount=2 Degree=1 IsPeriodic=0
  constraints (155):
    c: Coincident(g0,g1)
    c: Coincident(g1,g2)
    c: Coincident(g2,g3)
    c: Coincident(g3,g4)
    c: Coincident(g4,g5)
    c: Coincident(g5,g6)
    c: Coincident(g6,g7)
    c: Coincident(g7,g8)
    c: Coincident(g8,g9)
    c: Coincident(g9,g10)
    c: Coincident(g10,g11)
    c: Coincident(g11,g12)
    c: Coincident(g12,g0)
    c: Coincident(g13,g14)
    c: Coincident(g14,g15)
    c: Coincident(g15,g16)
    c: Coincident(g16,g17)
    c: Coincident(g17,g18)
    c: Coincident(g18,g19)
    c: Coincident(g19,g20)
    c: Coincident(g20,g21)
    c: Coincident(g21,g22)
    c: Coincident(g22,g23)
    c: Coincident(g23,g13)
    c: Coincident(g24,g25)
    c: Coincident(g25,g26)
    c: Coincident(g26,g27)
    c: Coincident(g27,g28)
    c: Coincident(g28,g29)
    c: Coincident(g29,g30)
    c: Coincident(g30,g31)
    c: Coincident(g31,g32)
    c: Coincident(g32,g33)
    c: Coincident(g33,g34)
    c: Coincident(g34,g35)
    c: Coincident(g35,g36)
    c: Coincident(g36,g37)
    c: Coincident(g37,g38)
    c: Coincident(g38,g39)
    c: Coincident(g39,g40)
    c: Coincident(g40,g41)
    c: Coincident(g41,g42)
    c: Coincident(g42,g43)
    c: Coincident(g43,g44)
    c: Coincident(g44,g45)
    c: Coincident(g45,g46)
    c: Coincident(g46,g47)
    c: Coincident(g47,g48)
    c: Coincident(g48,g49)
    c: Coincident(g49,g50)
    c: Coincident(g50,g51)
    c: Coincident(g51,g52)
    c: Coincident(g52,g24)
    c: Coincident(g53,g54)
    c: Coincident(g54,g55)
    c: Coincident(g55,g56)
    c: Coincident(g56,g57)
    c: Coincident(g57,g58)
    c: Coincident(g58,g59)
    c: Coincident(g59,g60)
    c: Coincident(g60,g61)
    c: Coincident(g61,g62)
    c: Coincident(g62,g63)
    c: Coincident(g63,g64)
    c: Coincident(g64,g65)
    c: Coincident(g65,g53)
    c: Coincident(g66,g67)
    c: Coincident(g67,g68)
    c: Coincident(g68,g69)
    c: Coincident(g69,g70)
    c: Coincident(g70,g71)
    c: Coincident(g71,g66)
    c: Coincident(g72,g73)
    c: Coincident(g73,g74)
    c: Coincident(g74,g75)
    c: Coincident(g75,g76)
    c: Coincident(g76,g77)
    c: Coincident(g77,g78)
    c: Coincident(g78,g72)
    c: Coincident(g79,g80)
    c: Coincident(g80,g81)
    c: Coincident(g81,g82)
    c: Coincident(g82,g83)
    c: Coincident(g83,g84)
    c: Coincident(g84,g85)
    c: Coincident(g85,g86)
    c: Coincident(g86,g87)
    c: Coincident(g87,g88)
    c: Coincident(g88,g89)
    c: Coincident(g89,g90)
    c: Coincident(g90,g79)
    c: Coincident(g91,g92)
    c: Coincident(g92,g93)
    c: Coincident(g93,g94)
    c: Coincident(g94,g95)
    c: Coincident(g95,g96)
    c: Coincident(g96,g97)
    c: Coincident(g97,g98)
    c: Coincident(g98,g99)
    c: Coincident(g99,g100)
    c: Coincident(g100,g101)
    c: Coincident(g101,g102)
    c: Coincident(g102,g103)
    c: Coincident(g103,g104)
    c: Coincident(g104,g91)
    c: Coincident(g105,g106)
    c: Coincident(g106,g107)
    c: Coincident(g107,g108)
    c: Coincident(g108,g109)
    c: Coincident(g109,g110)
    c: Coincident(g110,g111)
    c: Coincident(g111,g112)
    c: Coincident(g112,g105)
    c: Coincident(g113,g114)
    c: Coincident(g114,g115)
    c: Coincident(g115,g116)
    c: Coincident(g116,g117)
    c: Coincident(g117,g118)
    c: Coincident(g118,g119)
    c: Coincident(g119,g120)
    c: Coincident(g120,g121)
    c: Coincident(g121,g122)
    c: Coincident(g122,g113)
    c: Coincident(g123,g124)
    c: Coincident(g124,g125)
    c: Coincident(g125,g126)
    c: Coincident(g126,g127)
    c: Coincident(g127,g123)
    c: Coincident(g128,g129)
    c: Coincident(g129,g130)
    c: Coincident(g130,g131)
    c: Coincident(g131,g132)
    c: Coincident(g132,g128)
    c: Coincident(g133,g134)
    c: Coincident(g134,g135)
    c: Coincident(g135,g136)
    c: Coincident(g136,g137)
    c: Coincident(g137,g138)
    c: Coincident(g138,g139)
    c: Coincident(g139,g140)
    c: Coincident(g140,g141)
    c: Coincident(g141,g142)
    c: Coincident(g142,g143)
    c: Coincident(g143,g144)
    c: Coincident(g144,g145)
    c: Coincident(g145,g133)
    c: Coincident(g146,g147)
    c: Coincident(g147,g148)
    c: Coincident(g148,g149)
    c: Coincident(g149,g150)
    c: Coincident(g150,g151)
    c: Coincident(g151,g152)
    c: Coincident(g152,g153)
    c: Coincident(g153,g154)
    c: Coincident(g154,g146)
FEATURE [PartDesign::Pad] Pad021  label="Padresinident"
  BaseFeature = -> Pocket050
  Length = 0.2
  Length2 = 100
  Profile = -> Sketch162
  Type = 0
FEATURE [Sketcher::SketchObject] Sketch163
  ExternalGeometry = -> [Sketch]
  MapMode = 5
  Placement = pos=(0,0,4.3) rot=(0,0,1;0rad)
  expr: Placement.Base.z = Spreadsheet.floorthick + Spreadsheet.batthick - Spreadsheet.nutthick
  sketch-geometry (3):
    g0: Circle CenterX=-19.05 CenterY=28.75 CenterZ=0 NormalX=0 NormalY=0 NormalZ=1 AngleXU=0 Radius=1
    g1: Circle CenterX=19.05 CenterY=28.75 CenterZ=0 NormalX=0 NormalY=0 NormalZ=1 AngleXU=0 Radius=1
    g2: Circle CenterX=-1.27 CenterY=-22.05 CenterZ=0 NormalX=0 NormalY=0 NormalZ=1 AngleXU=0 Radius=1
  constraints (8):
    c: Radius(g0) = 1
    c: Radius(g1) = 1
    c: Radius(g2) = 1
    c: Symmetric(g0,g1,g-2)
    c: DistanceY(g0,g-3) = 3.25
    c: DistanceX(g0,g1) = 38.1
    c: DistanceX(g0,g2) = 17.78
    c: DistanceY(g2,g0) = 50.8
FEATURE [Sketcher::SketchObject] Sketch164
  AttachmentOffset = pos=(0,0,1.5) rot=(0,0,1;0rad)
  ExternalGeometry = -> [Sketch]
  MapMode = 5
  Placement = pos=(0,0,1.5) rot=(0,0,1;0rad)
  Support = -> [XY_Plane001]
  expr: Constraints[2] = Spreadsheet.nutrad + 2mm
  expr: Constraints[1] = Spreadsheet.nutrad + 2mm
  expr: AttachmentOffset.Base.z = Spreadsheet.floorthick
  expr: Constraints[0] = Spreadsheet.nutrad + 2mm
  sketch-geometry (3):
    g0: Circle CenterX=-19.05 CenterY=28.75 CenterZ=0 NormalX=0 NormalY=0 NormalZ=1 AngleXU=0 Radius=5.4
    g1: Circle CenterX=19.05 CenterY=28.75 CenterZ=0 NormalX=0 NormalY=0 NormalZ=1 AngleXU=0 Radius=5.4
    g2: Circle CenterX=-1.27 CenterY=-22.05 CenterZ=0 NormalX=0 NormalY=0 NormalZ=1 AngleXU=0 Radius=5.4
  constraints (8):
    c: Radius(g0) = 5.4
    c: Radius(g1) = 5.4
    c: Radius(g2) = 5.4
    c: DistanceY(g2,g0) = 50.8
    c: DistanceX(g0,g1) = 38.1
    c: DistanceX(g0,g2) = 17.78
    c: DistanceY(g0,g-3) = 3.25
    c: Symmetric(g0,g1,g-2)
FEATURE [PartDesign::Pad] Pad022  label="Padmntposts"
  BaseFeature = -> Pad021
  Length = 5.5
  Length2 = 100
  Profile = -> Sketch164
  Type = 0
  expr: Length = Spreadsheet.batthick
FEATURE [Sketcher::SketchObject] Sketch165
  AttachmentOffset = pos=(0,0,28.5) rot=(0,0,1;0rad)
  MapMode = 5
  Placement = pos=(0,-28.5,-6.3e-15) rot=(1,0,0;1.5708rad)
  Support = -> [XZ_Plane001]
  expr: Constraints[11] = Spreadsheet.floorthick
  expr: AttachmentOffset.Base.z = (Spreadsheet.caselength + Spreadsheet.pcboffset * 2) / 2 - 4mm
  expr: Constraints[10] = Spreadsheet.casewidth + Spreadsheet.pcboffset * 2
  expr: Constraints[9] = Spreadsheet.batthick
  expr: Constraints[4] = Spreadsheet.batthick
  sketch-geometry (6):
    g0: LineSegment StartX=-25.17 StartY=1.5 StartZ=0 EndX=-25.17 EndY=7 EndZ=0
    g1: LineSegment StartX=-25.17 StartY=7 StartZ=0 EndX=-27.17 EndY=1.5 EndZ=0
    g2: LineSegment StartX=-27.17 StartY=1.5 StartZ=0 EndX=-25.17 EndY=1.5 EndZ=0
    g3: LineSegment StartX=27.17 StartY=1.5 StartZ=0 EndX=25.17 EndY=7 EndZ=0
    g4: LineSegment StartX=25.17 StartY=7 StartZ=0 EndX=25.17 EndY=1.5 EndZ=0
    g5: LineSegment StartX=25.17 StartY=1.5 StartZ=0 EndX=27.17 EndY=1.5 EndZ=0
  constraints (17):
    c: Coincident(g0,g1)
    c: Coincident(g1,g2)
    c: Coincident(g2,g0)
    c: Horizontal(g2)
    c: DistanceY(g1,g0) = 5.5
    c: Coincident(g3,g4)
    c: Coincident(g4,g5)
    c: Coincident(g5,g3)
    c: Horizontal(g5)
    c: DistanceY(g4,g3) = 5.5
    c: DistanceX(g1,g3) = 54.34
    c: DistanceY(g-1,g1) = 1.5
    c: DistanceX(g1,g0) = 2
    c: Vertical(g0)
    c: Vertical(g4)
    c: DistanceX(g4,g3) = 2
    c: Symmetric(g4,g0,g-2)
FEATURE [Sketcher::SketchObject] Sketch166
  AttachmentOffset = pos=(0,0,7) rot=(0,0,1;0rad)
  ExternalGeometry = -> [Sketch]
  MapMode = 5
  Placement = pos=(0,0,7) rot=(0,0,1;0rad)
  Support = -> [XY_Plane001]
  expr: AttachmentOffset.Base.z = Spreadsheet.floorthick + Spreadsheet.batthick
  sketch-geometry (21):
    g0: LineSegment StartX=-17.45 StartY=25.9787 StartZ=0 EndX=-15.85 EndY=28.75 EndZ=0
    g1: LineSegment StartX=-15.85 StartY=28.75 StartZ=0 EndX=-17.45 EndY=31.5213 EndZ=0
    g2: LineSegment StartX=-17.45 StartY=31.5213 StartZ=0 EndX=-20.65 EndY=31.5213 EndZ=0
    g3: LineSegment StartX=-20.65 StartY=31.5213 StartZ=0 EndX=-22.25 EndY=28.75 EndZ=0
    g4: LineSegment StartX=-22.25 StartY=28.75 StartZ=0 EndX=-20.65 EndY=25.9787 EndZ=0
    g5: LineSegment StartX=-20.65 StartY=25.9787 StartZ=0 EndX=-17.45 EndY=25.9787 EndZ=0
    g6: Circle [constr] CenterX=-19.05 CenterY=28.75 CenterZ=0 NormalX=0 NormalY=0 NormalZ=1 AngleXU=0 Radius=3.2
    g7: LineSegment StartX=20.65 StartY=25.9787 StartZ=0 EndX=22.25 EndY=28.75 EndZ=0
    g8: LineSegment StartX=22.25 StartY=28.75 StartZ=0 EndX=20.65 EndY=31.5213 EndZ=0
    g9: LineSegment StartX=20.65 StartY=31.5213 StartZ=0 EndX=17.45 EndY=31.5213 EndZ=0
    g10: LineSegment StartX=17.45 StartY=31.5213 StartZ=0 EndX=15.85 EndY=28.75 EndZ=0
    g11: LineSegment StartX=15.85 StartY=28.75 StartZ=0 EndX=17.45 EndY=25.9787 EndZ=0
    g12: LineSegment StartX=17.45 StartY=25.9787 StartZ=0 EndX=20.65 EndY=25.9787 EndZ=0
    g13: Circle [constr] CenterX=19.05 CenterY=28.75 CenterZ=0 NormalX=0 NormalY=0 NormalZ=1 AngleXU=0 Radius=3.2
    g14: LineSegment StartX=0.33 StartY=-24.8213 StartZ=0 EndX=1.93 EndY=-22.05 EndZ=0
    g15: LineSegment StartX=1.93 StartY=-22.05 StartZ=0 EndX=0.33 EndY=-19.2787 EndZ=0
    g16: LineSegment StartX=0.33 StartY=-19.2787 StartZ=0 EndX=-2.87 EndY=-19.2787 EndZ=0
    g17: LineSegment StartX=-2.87 StartY=-19.2787 StartZ=0 EndX=-4.47 EndY=-22.05 EndZ=0
    g18: LineSegment StartX=-4.47 StartY=-22.05 StartZ=0 EndX=-2.87 EndY=-24.8213 EndZ=0
    g19: LineSegment StartX=-2.87 StartY=-24.8213 StartZ=0 EndX=0.33 EndY=-24.8213 EndZ=0
    g20: Circle [constr] CenterX=-1.27 CenterY=-22.05 CenterZ=0 NormalX=0 NormalY=0 NormalZ=1 AngleXU=0 Radius=3.2
  constraints (50):
    c: Coincident(g0,g1)
    c: Coincident(g1,g2)
    c: Coincident(g2,g3)
    c: Coincident(g3,g4)
    c: Coincident(g4,g5)
    c: Coincident(g5,g0)
    c: Equal(g0, g1-g5) x5
    c: PointOnObject(g0,g6)
    c: PointOnObject(g1,g6)
    c: PointOnObject(g2,g6)
    c: PointOnObject(g3,g6)
    c: PointOnObject(g4,g6)
    c: PointOnObject(g5,g6)
    c: Coincident(g7,g8)
    c: Coincident(g8,g9)
    c: Coincident(g9,g10)
    c: Coincident(g10,g11)
    c: Coincident(g11,g12)
    c: Coincident(g12,g7)
    c: Equal(g7, g8-g12) x5
    c: PointOnObject(g7,g13)
    c: PointOnObject(g8,g13)
    c: PointOnObject(g9,g13)
    c: PointOnObject(g10,g13)
    c: PointOnObject(g11,g13)
    c: PointOnObject(g12,g13)
    c: Coincident(g14,g15)
    c: Coincident(g15,g16)
    c: Coincident(g16,g17)
    c: Coincident(g17,g18)
    c: Coincident(g18,g19)
    c: Coincident(g19,g14)
    c: Equal(g14, g15-g19) x5
    c: PointOnObject(g14,g20)
    c: PointOnObject(g15,g20)
    c: PointOnObject(g16,g20)
    c: PointOnObject(g17,g20)
    c: PointOnObject(g18,g20)
    c: PointOnObject(g19,g20)
    c: Horizontal(g5)
    c: Horizontal(g19)
    c: Horizontal(g12)
    c: Symmetric(g6,g13,g-2)
    c: DistanceY(g6,g-3) = 3.25
    c: DistanceY(g20,g6) = 50.8
    c: DistanceX(g6,g13) = 38.1
    c: DistanceX(g6,g20) = 17.78
    c: Diameter(g6) = 6.4
    c: Diameter(g13) = 6.4
    c: Diameter(g20) = 6.4
FEATURE [PartDesign::Pocket] Pocket053  label="Pockhexnuts"
  BaseFeature = -> Pad022
  Length = 2.7
  Length2 = 100
  Profile = -> Sketch166
  Type = 0
  expr: Length = Spreadsheet.nutthick
FEATURE [PartDesign::Pocket] Pocket051  label="Pockhexholes"
  BaseFeature = -> Pocket053
  Length = 1
  Length2 = 100
  Profile = -> Sketch163
  Type = 0
FEATURE [PartDesign::Pad] Pad023  label="Padsidesupprt"
  BaseFeature = -> Pocket051
  Length = 5.5
  Length2 = 100
  Profile = -> Sketch014
  Type = 0
  expr: Length = Spreadsheet.batthick
FEATURE [PartDesign::Pocket] Pocket052  label="Pocksidesupprt"
  BaseFeature = -> Pad023
  Length = 4
  Length2 = 100
  Profile = -> Sketch165
  Type = 0
FEATURE [PartDesign::Fillet] Fillet  label="Filltwallin"
  Base = -> Pocket052 [Edge433,Edge709,Edge536,Edge429]
  BaseFeature = -> Pocket052
  Radius = 2
FEATURE [PartDesign::Fillet] Fillet003  label="Filltwallmid"
  Base = -> Fillet [Edge257,Edge259,Edge255,Edge251]
  BaseFeature = -> Fillet
  Radius = 3
FEATURE [PartDesign::Fillet] Fillet004  label="Filltwallout"
  Base = -> Fillet003 [Edge358,Edge352,Edge346,Edge345]
  BaseFeature = -> Fillet003
  Radius = 4
FEATURE [PartDesign::Fillet] Fillet005  label="Filltpwrswtch"
  Base = -> Fillet004 [Edge58,Edge57,Edge60,Edge59]
  BaseFeature = -> Fillet004
  Radius = 1
FEATURE [PartDesign::Fillet] Fillet006  label="Filltetiket"
  Base = -> Fillet005 [Edge410,Edge406,Edge405,Edge408]
  BaseFeature = -> Fillet005
  Radius = 2
FEATURE [PartDesign::Body] Body  label="Bodybox"
  Group = -> [Sketch,Sketch001,Pad,Sketch002,Pocket,Sketch003,Pocket001,Sketch005,Pocket002,Sketch007,Pad003,Sketch009,Pocket003,Sketch010,Pad006,Sketch011,Pocket004,Sketch012,Pocket005,Sketch013,Pocket006,Sketch014,Sketch016,Sketch017,Pocket009,Sketch018,Pocket010,Pocket011,ShapeString,Sketch136,Pocket045,Sketch137,Pocket046,Sketch138,Pocket047,Sketch139,Pocket048,Sketch140,Pocket049,Sketch141,Pocket050,+16 more]
  Origin = -> Origin001
  Tip = -> Fillet006
FEATURE [App::Part] Part  label="Mainpart"
  Group = -> [Body]
  Origin = -> Origin
FEATURE [TechDraw::DrawViewPart] View  label="Viewtop"
  CoarseView = false
  Direction = (0,0,1)
  Focus = 100
  HardHidden = false
  IsoCount = 0
  IsoHidden = false
  IsoVisible = false
  LockPosition = false
  Perspective = false
  Rotation = 0
  ScaleType = 0
  SeamHidden = false
  SeamVisible = false
  SmoothHidden = false
  SmoothVisible = false
  Source = -> [Part]
  X = 211.005
  Y = 128.383
FEATURE [TechDraw::DrawViewPart] View001  label="Viewfrnt"
  CoarseView = false
  Direction = (0,-1,0)
  Focus = 100
  HardHidden = false
  IsoCount = 0
  IsoHidden = false
  IsoVisible = false
  LockPosition = false
  Perspective = false
  Rotation = 0
  ScaleType = 0
  SeamHidden = false
  SeamVisible = false
  SmoothHidden = false
  SmoothVisible = false
  Source = -> [Part]
  X = 78.7998
  Y = 158.512
FEATURE [TechDraw::DrawViewPart] View002  label="Viewiso"
  CoarseView = false
  Direction = (0.577,-0.577,0.577)
  Focus = 100
  HardHidden = false
  IsoCount = 0
  IsoHidden = false
  IsoVisible = false
  LockPosition = false
  Perspective = false
  Rotation = 0
  ScaleType = 0
  SeamHidden = false
  SeamVisible = false
  SmoothHidden = false
  SmoothVisible = false
  Source = -> [Part]
  X = 79.6991
  Y = 69.0257
FEATURE [TechDraw::DrawPage] Page
  KeepUpdated = true
  ProjectionType = 0
  Template = -> Template
  Views = -> [View001,View002,View,Symbol]
FEATURE [Mesh::Feature] Mesh238  label="Meshtextgreen"
FEATURE [Mesh::Feature] Mesh245  label="Meshmonrand"
FEATURE [Mesh::Feature] Mesh252  label="Meshtextmon"
FEATURE [Mesh::Feature] Mesh253  label="Meshetikette"
FEATURE [Mesh::Feature] Mesh  label="Meshmainbod"
